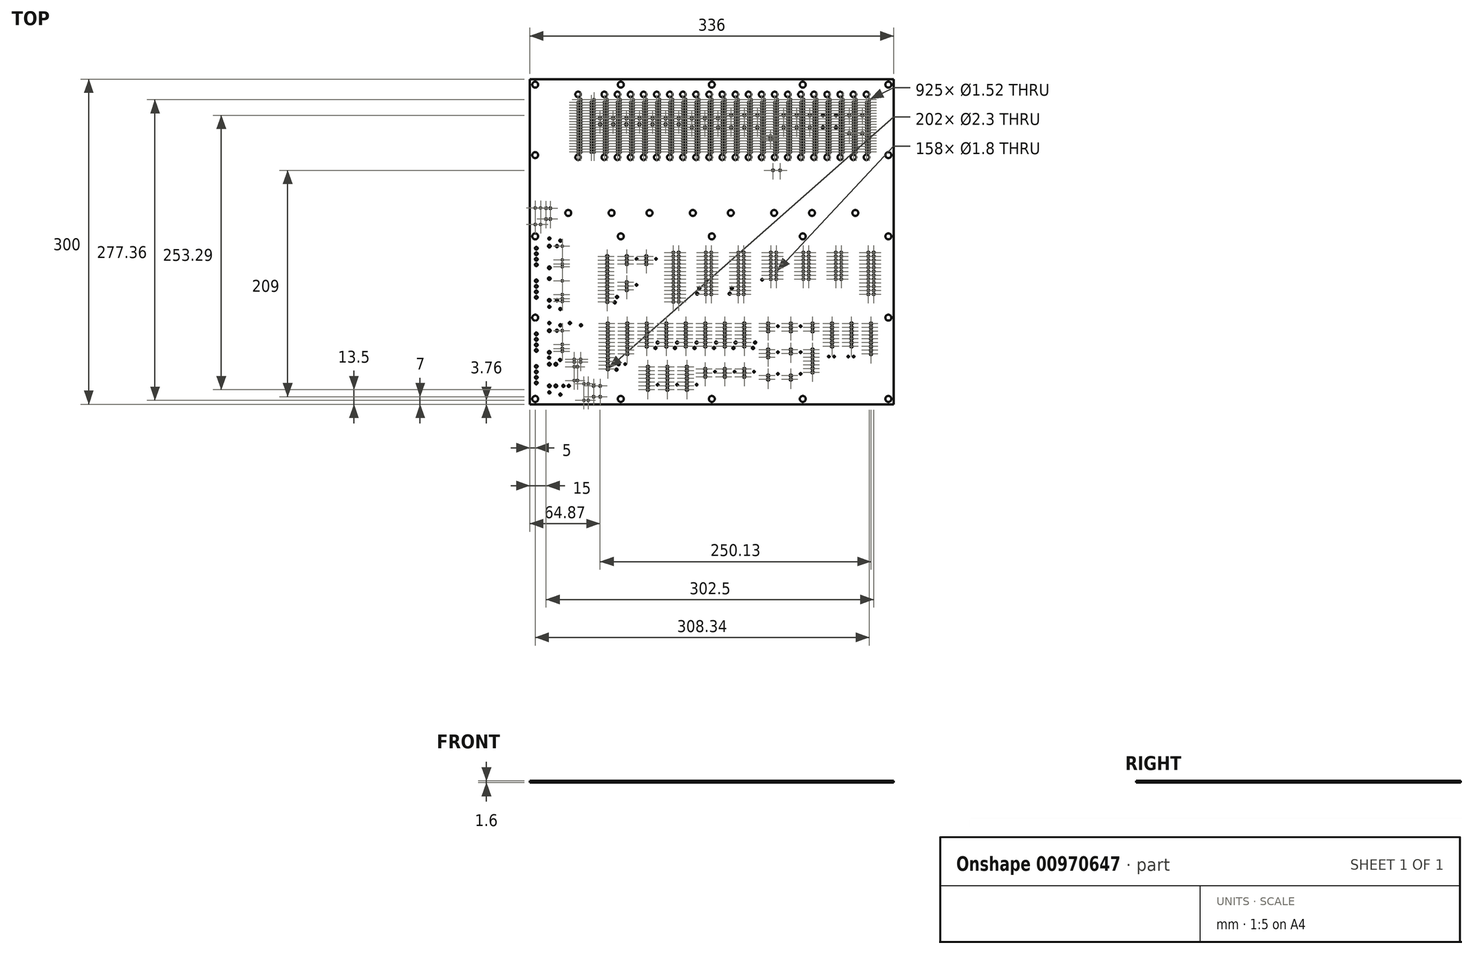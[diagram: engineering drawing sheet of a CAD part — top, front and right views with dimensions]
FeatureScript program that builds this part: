
annotation { "Feature Type Name" : "Feature", "Feature Type Description" : "" }
export const myFeature = defineFeature(function(context is Context, id is Id, definition is map)
    precondition{}
    {
        {
            var Q0;
            Q0=qCreatedBy(makeId("Top.planeOp"),FACE);
            var sketch = newSketch(context, id + "F0", { "sketchPlane" : qUnion([Q0])});
            skCircle(sketch, "E0", {"center": v(-149, 21) * mm, "radius": 0.9 * mm});
            skCircle(sketch, "E1", {"center": v(-149, 31) * mm, "radius": 0.9 * mm});
            skCircle(sketch, "E2", {"center": v(-153, 21) * mm, "radius": 0.9 * mm});
            skCircle(sketch, "E3", {"center": v(-153, 31) * mm, "radius": 0.9 * mm});
            skCircle(sketch, "E4", {"center": v(-103, -133) * mm, "radius": 0.9 * mm});
            skCircle(sketch, "E5", {"center": v(-103, -143) * mm, "radius": 0.9 * mm});
            skCircle(sketch, "E6", {"center": v(-109, -133) * mm, "radius": 0.9 * mm});
            skCircle(sketch, "E7", {"center": v(-109, -143) * mm, "radius": 0.9 * mm});
            skCircle(sketch, "E8", {"center": v(63, 66) * mm, "radius": 0.9 * mm});
            skCircle(sketch, "E9", {"center": v(56.5, 66) * mm, "radius": 0.9 * mm});
            skCircle(sketch, "E10", {"center": v(-162, -6) * mm, "radius": 1.27 * mm});
            skCircle(sketch, "E11", {"center": v(-162, -11.08) * mm, "radius": 1.27 * mm});
            skCircle(sketch, "E12", {"center": v(-162, -16.16) * mm, "radius": 1.27 * mm});
            skCircle(sketch, "E13", {"center": v(-162, -21.24) * mm, "radius": 1.27 * mm});
            skCircle(sketch, "E14", {"center": v(-162, -85) * mm, "radius": 1.27 * mm});
            skCircle(sketch, "E15", {"center": v(-162, -90.08) * mm, "radius": 1.27 * mm});
            skCircle(sketch, "E16", {"center": v(-162, -95.16) * mm, "radius": 1.27 * mm});
            skCircle(sketch, "E17", {"center": v(-162, -100.24) * mm, "radius": 1.27 * mm});
            skCircle(sketch, "E18", {"center": v(-162, -115) * mm, "radius": 1.27 * mm});
            skCircle(sketch, "E19", {"center": v(-162, -120.08) * mm, "radius": 1.27 * mm});
            skCircle(sketch, "E20", {"center": v(-162, -125.16) * mm, "radius": 1.27 * mm});
            skCircle(sketch, "E21", {"center": v(-162, -130.24) * mm, "radius": 1.27 * mm});
            skCircle(sketch, "E22", {"center": v(-162, -36) * mm, "radius": 1.27 * mm});
            skCircle(sketch, "E23", {"center": v(-162, -41.08) * mm, "radius": 1.27 * mm});
            skCircle(sketch, "E24", {"center": v(-162, -46.16) * mm, "radius": 1.27 * mm});
            skCircle(sketch, "E25", {"center": v(-162, -51.24) * mm, "radius": 1.27 * mm});
            skCircle(sketch, "E26", {"center": v(-78.5, -13.4) * mm, "radius": 1.15 * mm});
            skCircle(sketch, "E27", {"center": v(-78.5, -16.9) * mm, "radius": 1.15 * mm});
            skCircle(sketch, "E28", {"center": v(-78.5, -20.4) * mm, "radius": 1.15 * mm});
            skCircle(sketch, "E29", {"center": v(-60.5, -13.4) * mm, "radius": 1.15 * mm});
            skCircle(sketch, "E30", {"center": v(-60.5, -16.9) * mm, "radius": 1.15 * mm});
            skCircle(sketch, "E31", {"center": v(-60.5, -20.4) * mm, "radius": 1.15 * mm});
            skCircle(sketch, "E32", {"center": v(-78.5, -37.4) * mm, "radius": 1.15 * mm});
            skCircle(sketch, "E33", {"center": v(-78.5, -40.9) * mm, "radius": 1.15 * mm});
            skCircle(sketch, "E34", {"center": v(-78.5, -44.4) * mm, "radius": 1.15 * mm});
            skCircle(sketch, "E35", {"center": v(-96.5, -13.4) * mm, "radius": 1.15 * mm});
            skCircle(sketch, "E36", {"center": v(-96.5, -16.9) * mm, "radius": 1.15 * mm});
            skCircle(sketch, "E37", {"center": v(-96.5, -20.4) * mm, "radius": 1.15 * mm});
            skCircle(sketch, "E38", {"center": v(-96.5, -23.9) * mm, "radius": 1.15 * mm});
            skCircle(sketch, "E39", {"center": v(-96.5, -27.4) * mm, "radius": 1.15 * mm});
            skCircle(sketch, "E40", {"center": v(-96.5, -30.9) * mm, "radius": 1.15 * mm});
            skCircle(sketch, "E41", {"center": v(-96.5, -34.4) * mm, "radius": 1.15 * mm});
            skCircle(sketch, "E42", {"center": v(-96.5, -37.9) * mm, "radius": 1.15 * mm});
            skCircle(sketch, "E43", {"center": v(-96.5, -41.4) * mm, "radius": 1.15 * mm});
            skCircle(sketch, "E44", {"center": v(-96.5, -44.9) * mm, "radius": 1.15 * mm});
            skCircle(sketch, "E45", {"center": v(-96.5, -48.4) * mm, "radius": 1.15 * mm});
            skCircle(sketch, "E46", {"center": v(-96.5, -51.9) * mm, "radius": 1.15 * mm});
            skCircle(sketch, "E47", {"center": v(-96.5, -55.4) * mm, "radius": 1.15 * mm});
            skCircle(sketch, "E48", {"center": v(-78, -75.5) * mm, "radius": 1.15 * mm});
            skCircle(sketch, "E49", {"center": v(-78, -79) * mm, "radius": 1.15 * mm});
            skCircle(sketch, "E50", {"center": v(-78, -82.5) * mm, "radius": 1.15 * mm});
            skCircle(sketch, "E51", {"center": v(-78, -86) * mm, "radius": 1.15 * mm});
            skCircle(sketch, "E52", {"center": v(-78, -89.5) * mm, "radius": 1.15 * mm});
            skCircle(sketch, "E53", {"center": v(-78, -93) * mm, "radius": 1.15 * mm});
            skCircle(sketch, "E54", {"center": v(-78, -96.5) * mm, "radius": 1.15 * mm});
            skCircle(sketch, "E55", {"center": v(-78, -100) * mm, "radius": 1.15 * mm});
            skCircle(sketch, "E56", {"center": v(-78, -103.5) * mm, "radius": 1.15 * mm});
            skCircle(sketch, "E57", {"center": v(-60, -75.5) * mm, "radius": 1.15 * mm});
            skCircle(sketch, "E58", {"center": v(-60, -79) * mm, "radius": 1.15 * mm});
            skCircle(sketch, "E59", {"center": v(-60, -82.5) * mm, "radius": 1.15 * mm});
            skCircle(sketch, "E60", {"center": v(-60, -86) * mm, "radius": 1.15 * mm});
            skCircle(sketch, "E61", {"center": v(-60, -89.5) * mm, "radius": 1.15 * mm});
            skCircle(sketch, "E62", {"center": v(-60, -93) * mm, "radius": 1.15 * mm});
            skCircle(sketch, "E63", {"center": v(-60, -96.5) * mm, "radius": 1.15 * mm});
            skCircle(sketch, "E64", {"center": v(-42, -75.5) * mm, "radius": 1.15 * mm});
            skCircle(sketch, "E65", {"center": v(-42, -79) * mm, "radius": 1.15 * mm});
            skCircle(sketch, "E66", {"center": v(-42, -82.5) * mm, "radius": 1.15 * mm});
            skCircle(sketch, "E67", {"center": v(-42, -86) * mm, "radius": 1.15 * mm});
            skCircle(sketch, "E68", {"center": v(-42, -89.5) * mm, "radius": 1.15 * mm});
            skCircle(sketch, "E69", {"center": v(-42, -93) * mm, "radius": 1.15 * mm});
            skCircle(sketch, "E70", {"center": v(-42, -96.5) * mm, "radius": 1.15 * mm});
            skCircle(sketch, "E71", {"center": v(-24, -75.5) * mm, "radius": 1.15 * mm});
            skCircle(sketch, "E72", {"center": v(-24, -79) * mm, "radius": 1.15 * mm});
            skCircle(sketch, "E73", {"center": v(-24, -82.5) * mm, "radius": 1.15 * mm});
            skCircle(sketch, "E74", {"center": v(-24, -86) * mm, "radius": 1.15 * mm});
            skCircle(sketch, "E75", {"center": v(-24, -89.5) * mm, "radius": 1.15 * mm});
            skCircle(sketch, "E76", {"center": v(-24, -93) * mm, "radius": 1.15 * mm});
            skCircle(sketch, "E77", {"center": v(-24, -96.5) * mm, "radius": 1.15 * mm});
            skCircle(sketch, "E78", {"center": v(-6, -75.5) * mm, "radius": 1.15 * mm});
            skCircle(sketch, "E79", {"center": v(-6, -79) * mm, "radius": 1.15 * mm});
            skCircle(sketch, "E80", {"center": v(-6, -82.5) * mm, "radius": 1.15 * mm});
            skCircle(sketch, "E81", {"center": v(-6, -86) * mm, "radius": 1.15 * mm});
            skCircle(sketch, "E82", {"center": v(-6, -89.5) * mm, "radius": 1.15 * mm});
            skCircle(sketch, "E83", {"center": v(-6, -93) * mm, "radius": 1.15 * mm});
            skCircle(sketch, "E84", {"center": v(-6, -96.5) * mm, "radius": 1.15 * mm});
            skCircle(sketch, "E85", {"center": v(12, -75.5) * mm, "radius": 1.15 * mm});
            skCircle(sketch, "E86", {"center": v(12, -79) * mm, "radius": 1.15 * mm});
            skCircle(sketch, "E87", {"center": v(12, -82.5) * mm, "radius": 1.15 * mm});
            skCircle(sketch, "E88", {"center": v(12, -86) * mm, "radius": 1.15 * mm});
            skCircle(sketch, "E89", {"center": v(12, -89.5) * mm, "radius": 1.15 * mm});
            skCircle(sketch, "E90", {"center": v(12, -93) * mm, "radius": 1.15 * mm});
            skCircle(sketch, "E91", {"center": v(12, -96.5) * mm, "radius": 1.15 * mm});
            skCircle(sketch, "E92", {"center": v(30, -75.5) * mm, "radius": 1.15 * mm});
            skCircle(sketch, "E93", {"center": v(30, -79) * mm, "radius": 1.15 * mm});
            skCircle(sketch, "E94", {"center": v(30, -82.5) * mm, "radius": 1.15 * mm});
            skCircle(sketch, "E95", {"center": v(30, -86) * mm, "radius": 1.15 * mm});
            skCircle(sketch, "E96", {"center": v(30, -89.5) * mm, "radius": 1.15 * mm});
            skCircle(sketch, "E97", {"center": v(30, -93) * mm, "radius": 1.15 * mm});
            skCircle(sketch, "E98", {"center": v(30, -96.5) * mm, "radius": 1.15 * mm});
            skCircle(sketch, "E99", {"center": v(-96, -75.5) * mm, "radius": 1.15 * mm});
            skCircle(sketch, "E100", {"center": v(-96, -79) * mm, "radius": 1.15 * mm});
            skCircle(sketch, "E101", {"center": v(-96, -82.5) * mm, "radius": 1.15 * mm});
            skCircle(sketch, "E102", {"center": v(-96, -86) * mm, "radius": 1.15 * mm});
            skCircle(sketch, "E103", {"center": v(-96, -89.5) * mm, "radius": 1.15 * mm});
            skCircle(sketch, "E104", {"center": v(-96, -93) * mm, "radius": 1.15 * mm});
            skCircle(sketch, "E105", {"center": v(-96, -96.5) * mm, "radius": 1.15 * mm});
            skCircle(sketch, "E106", {"center": v(-96, -100) * mm, "radius": 1.15 * mm});
            skCircle(sketch, "E107", {"center": v(-96, -103.5) * mm, "radius": 1.15 * mm});
            skCircle(sketch, "E108", {"center": v(-96, -107) * mm, "radius": 1.15 * mm});
            skCircle(sketch, "E109", {"center": v(-96, -110.5) * mm, "radius": 1.15 * mm});
            skCircle(sketch, "E110", {"center": v(-96, -114) * mm, "radius": 1.15 * mm});
            skCircle(sketch, "E111", {"center": v(-96, -117.5) * mm, "radius": 1.15 * mm});
            skCircle(sketch, "E112", {"center": v(-6, -117.5) * mm, "radius": 1.15 * mm});
            skCircle(sketch, "E113", {"center": v(-6, -121) * mm, "radius": 1.15 * mm});
            skCircle(sketch, "E114", {"center": v(-6, -124.5) * mm, "radius": 1.15 * mm});
            skCircle(sketch, "E115", {"center": v(12, -117.5) * mm, "radius": 1.15 * mm});
            skCircle(sketch, "E116", {"center": v(12, -121) * mm, "radius": 1.15 * mm});
            skCircle(sketch, "E117", {"center": v(12, -124.5) * mm, "radius": 1.15 * mm});
            skCircle(sketch, "E118", {"center": v(30, -117.5) * mm, "radius": 1.15 * mm});
            skCircle(sketch, "E119", {"center": v(30, -121) * mm, "radius": 1.15 * mm});
            skCircle(sketch, "E120", {"center": v(30, -124.5) * mm, "radius": 1.15 * mm});
            skCircle(sketch, "E121", {"center": v(52, -75.5) * mm, "radius": 1.15 * mm});
            skCircle(sketch, "E122", {"center": v(52, -79) * mm, "radius": 1.15 * mm});
            skCircle(sketch, "E123", {"center": v(52, -82.5) * mm, "radius": 1.15 * mm});
            skCircle(sketch, "E124", {"center": v(73, -75.5) * mm, "radius": 1.15 * mm});
            skCircle(sketch, "E125", {"center": v(73, -79) * mm, "radius": 1.15 * mm});
            skCircle(sketch, "E126", {"center": v(73, -82.5) * mm, "radius": 1.15 * mm});
            skCircle(sketch, "E127", {"center": v(52, -99.5) * mm, "radius": 1.15 * mm});
            skCircle(sketch, "E128", {"center": v(52, -103) * mm, "radius": 1.15 * mm});
            skCircle(sketch, "E129", {"center": v(52, -106.5) * mm, "radius": 1.15 * mm});
            skCircle(sketch, "E130", {"center": v(73, -99.5) * mm, "radius": 1.15 * mm});
            skCircle(sketch, "E131", {"center": v(73, -103) * mm, "radius": 1.15 * mm});
            skCircle(sketch, "E132", {"center": v(52, -123.5) * mm, "radius": 1.15 * mm});
            skCircle(sketch, "E133", {"center": v(52, -127) * mm, "radius": 1.15 * mm});
            skCircle(sketch, "E134", {"center": v(73, -123.5) * mm, "radius": 1.15 * mm});
            skCircle(sketch, "E135", {"center": v(73, -127) * mm, "radius": 1.15 * mm});
            skCircle(sketch, "E136", {"center": v(-59, -115.5) * mm, "radius": 1.15 * mm});
            skCircle(sketch, "E137", {"center": v(-59, -119) * mm, "radius": 1.15 * mm});
            skCircle(sketch, "E138", {"center": v(-59, -122.5) * mm, "radius": 1.15 * mm});
            skCircle(sketch, "E139", {"center": v(-59, -126) * mm, "radius": 1.15 * mm});
            skCircle(sketch, "E140", {"center": v(-59, -129.5) * mm, "radius": 1.15 * mm});
            skCircle(sketch, "E141", {"center": v(-59, -133) * mm, "radius": 1.15 * mm});
            skCircle(sketch, "E142", {"center": v(-59, -136.5) * mm, "radius": 1.15 * mm});
            skCircle(sketch, "E143", {"center": v(-23, -115.5) * mm, "radius": 1.15 * mm});
            skCircle(sketch, "E144", {"center": v(-23, -119) * mm, "radius": 1.15 * mm});
            skCircle(sketch, "E145", {"center": v(-23, -122.5) * mm, "radius": 1.15 * mm});
            skCircle(sketch, "E146", {"center": v(-23, -126) * mm, "radius": 1.15 * mm});
            skCircle(sketch, "E147", {"center": v(-23, -129.5) * mm, "radius": 1.15 * mm});
            skCircle(sketch, "E148", {"center": v(-23, -133) * mm, "radius": 1.15 * mm});
            skCircle(sketch, "E149", {"center": v(-23, -136.5) * mm, "radius": 1.15 * mm});
            skCircle(sketch, "E150", {"center": v(-41, -115.5) * mm, "radius": 1.15 * mm});
            skCircle(sketch, "E151", {"center": v(-41, -119) * mm, "radius": 1.15 * mm});
            skCircle(sketch, "E152", {"center": v(-41, -122.5) * mm, "radius": 1.15 * mm});
            skCircle(sketch, "E153", {"center": v(-41, -126) * mm, "radius": 1.15 * mm});
            skCircle(sketch, "E154", {"center": v(-41, -129.5) * mm, "radius": 1.15 * mm});
            skCircle(sketch, "E155", {"center": v(-41, -133) * mm, "radius": 1.15 * mm});
            skCircle(sketch, "E156", {"center": v(-41, -136.5) * mm, "radius": 1.15 * mm});
            skCircle(sketch, "E157", {"center": v(93, -75.5) * mm, "radius": 1.15 * mm});
            skCircle(sketch, "E158", {"center": v(93, -79) * mm, "radius": 1.15 * mm});
            skCircle(sketch, "E159", {"center": v(93, -82.5) * mm, "radius": 1.15 * mm});
            skCircle(sketch, "E160", {"center": v(111, -75.5) * mm, "radius": 1.15 * mm});
            skCircle(sketch, "E161", {"center": v(111, -79) * mm, "radius": 1.15 * mm});
            skCircle(sketch, "E162", {"center": v(111, -82.5) * mm, "radius": 1.15 * mm});
            skCircle(sketch, "E163", {"center": v(111, -86) * mm, "radius": 1.15 * mm});
            skCircle(sketch, "E164", {"center": v(111, -89.5) * mm, "radius": 1.15 * mm});
            skCircle(sketch, "E165", {"center": v(111, -93) * mm, "radius": 1.15 * mm});
            skCircle(sketch, "E166", {"center": v(111, -96.5) * mm, "radius": 1.15 * mm});
            skCircle(sketch, "E167", {"center": v(129, -75.5) * mm, "radius": 1.15 * mm});
            skCircle(sketch, "E168", {"center": v(129, -79) * mm, "radius": 1.15 * mm});
            skCircle(sketch, "E169", {"center": v(129, -82.5) * mm, "radius": 1.15 * mm});
            skCircle(sketch, "E170", {"center": v(129, -86) * mm, "radius": 1.15 * mm});
            skCircle(sketch, "E171", {"center": v(129, -89.5) * mm, "radius": 1.15 * mm});
            skCircle(sketch, "E172", {"center": v(129, -93) * mm, "radius": 1.15 * mm});
            skCircle(sketch, "E173", {"center": v(129, -96.5) * mm, "radius": 1.15 * mm});
            skCircle(sketch, "E174", {"center": v(147, -75.5) * mm, "radius": 1.15 * mm});
            skCircle(sketch, "E175", {"center": v(147, -79) * mm, "radius": 1.15 * mm});
            skCircle(sketch, "E176", {"center": v(147, -82.5) * mm, "radius": 1.15 * mm});
            skCircle(sketch, "E177", {"center": v(147, -86) * mm, "radius": 1.15 * mm});
            skCircle(sketch, "E178", {"center": v(147, -89.5) * mm, "radius": 1.15 * mm});
            skCircle(sketch, "E179", {"center": v(147, -93) * mm, "radius": 1.15 * mm});
            skCircle(sketch, "E180", {"center": v(147, -96.5) * mm, "radius": 1.15 * mm});
            skCircle(sketch, "E181", {"center": v(147, -100) * mm, "radius": 1.15 * mm});
            skCircle(sketch, "E182", {"center": v(147, -103.5) * mm, "radius": 1.15 * mm});
            skCircle(sketch, "E183", {"center": v(93, -99.5) * mm, "radius": 1.15 * mm});
            skCircle(sketch, "E184", {"center": v(93, -103) * mm, "radius": 1.15 * mm});
            skCircle(sketch, "E185", {"center": v(93, -106.5) * mm, "radius": 1.15 * mm});
            skCircle(sketch, "E186", {"center": v(93, -110) * mm, "radius": 1.15 * mm});
            skCircle(sketch, "E187", {"center": v(93, -113.5) * mm, "radius": 1.15 * mm});
            skCircle(sketch, "E188", {"center": v(93, -117) * mm, "radius": 1.15 * mm});
            skCircle(sketch, "E189", {"center": v(93, -120.5) * mm, "radius": 1.15 * mm});
            skCircle(sketch, "E190", {"center": v(-18.43, 114) * mm, "radius": 1.15 * mm});
            skCircle(sketch, "E191", {"center": v(-18.43, 105.6) * mm, "radius": 1.15 * mm});
            skCircle(sketch, "E192", {"center": v(5.77, 114) * mm, "radius": 1.15 * mm});
            skCircle(sketch, "E193", {"center": v(5.77, 105.6) * mm, "radius": 1.15 * mm});
            skCircle(sketch, "E194", {"center": v(17.87, 116.79) * mm, "radius": 1.15 * mm});
            skCircle(sketch, "E195", {"center": v(17.87, 105.6) * mm, "radius": 1.15 * mm});
            skCircle(sketch, "E196", {"center": v(29.97, 116.79) * mm, "radius": 1.15 * mm});
            skCircle(sketch, "E197", {"center": v(29.97, 105.6) * mm, "radius": 1.15 * mm});
            skCircle(sketch, "E198", {"center": v(42.07, 116.79) * mm, "radius": 1.15 * mm});
            skCircle(sketch, "E199", {"center": v(42.07, 105.6) * mm, "radius": 1.15 * mm});
            skCircle(sketch, "E200", {"center": v(54.17, 97.2) * mm, "radius": 1.15 * mm});
            skCircle(sketch, "E201", {"center": v(54.17, 94.39) * mm, "radius": 1.15 * mm});
            skCircle(sketch, "E202", {"center": v(66.27, 116.79) * mm, "radius": 1.15 * mm});
            skCircle(sketch, "E203", {"center": v(66.27, 105.6) * mm, "radius": 1.15 * mm});
            skCircle(sketch, "E204", {"center": v(-6.33, 114) * mm, "radius": 1.15 * mm});
            skCircle(sketch, "E205", {"center": v(-6.33, 105.6) * mm, "radius": 1.15 * mm});
            skCircle(sketch, "E206", {"center": v(78.37, 116.79) * mm, "radius": 1.15 * mm});
            skCircle(sketch, "E207", {"center": v(78.37, 105.6) * mm, "radius": 1.15 * mm});
            skCircle(sketch, "E208", {"center": v(90.47, 116.79) * mm, "radius": 1.15 * mm});
            skCircle(sketch, "E209", {"center": v(90.47, 105.6) * mm, "radius": 1.15 * mm});
            skCircle(sketch, "E210", {"center": v(-103.13, 114) * mm, "radius": 1.15 * mm});
            skCircle(sketch, "E211", {"center": v(-103.13, 108.39) * mm, "radius": 1.15 * mm});
            skCircle(sketch, "E212", {"center": v(126.8, 116.79) * mm, "radius": 1.15 * mm});
            skCircle(sketch, "E213", {"center": v(126.8, 99.99) * mm, "radius": 1.15 * mm});
            skCircle(sketch, "E214", {"center": v(138.9, 116.79) * mm, "radius": 1.15 * mm});
            skCircle(sketch, "E215", {"center": v(138.9, 99.99) * mm, "radius": 1.15 * mm});
            skCircle(sketch, "E216", {"center": v(-91.03, 114) * mm, "radius": 1.15 * mm});
            skCircle(sketch, "E217", {"center": v(-91.03, 108.39) * mm, "radius": 1.15 * mm});
            skCircle(sketch, "E218", {"center": v(-78.93, 114) * mm, "radius": 1.15 * mm});
            skCircle(sketch, "E219", {"center": v(-78.93, 108.39) * mm, "radius": 1.15 * mm});
            skCircle(sketch, "E220", {"center": v(-66.83, 114) * mm, "radius": 1.15 * mm});
            skCircle(sketch, "E221", {"center": v(-66.83, 108.39) * mm, "radius": 1.15 * mm});
            skCircle(sketch, "E222", {"center": v(-54.73, 114) * mm, "radius": 1.15 * mm});
            skCircle(sketch, "E223", {"center": v(-54.73, 108.39) * mm, "radius": 1.15 * mm});
            skCircle(sketch, "E224", {"center": v(-42.63, 114) * mm, "radius": 1.15 * mm});
            skCircle(sketch, "E225", {"center": v(-42.63, 108.39) * mm, "radius": 1.15 * mm});
            skCircle(sketch, "E226", {"center": v(-30.53, 114) * mm, "radius": 1.15 * mm});
            skCircle(sketch, "E227", {"center": v(-30.53, 108.39) * mm, "radius": 1.15 * mm});
            skCircle(sketch, "E228", {"center": v(-30.5, -9.9) * mm, "radius": 0.9 * mm});
            skCircle(sketch, "E229", {"center": v(-30.5, -13.4) * mm, "radius": 0.9 * mm});
            skCircle(sketch, "E230", {"center": v(-30.5, -16.9) * mm, "radius": 0.9 * mm});
            skCircle(sketch, "E231", {"center": v(-30.5, -20.4) * mm, "radius": 0.9 * mm});
            skCircle(sketch, "E232", {"center": v(-30.5, -23.9) * mm, "radius": 0.9 * mm});
            skCircle(sketch, "E233", {"center": v(-30.5, -27.4) * mm, "radius": 0.9 * mm});
            skCircle(sketch, "E234", {"center": v(-30.5, -30.9) * mm, "radius": 0.9 * mm});
            skCircle(sketch, "E235", {"center": v(-30.5, -34.4) * mm, "radius": 0.9 * mm});
            skCircle(sketch, "E236", {"center": v(-30.5, -37.9) * mm, "radius": 0.9 * mm});
            skCircle(sketch, "E237", {"center": v(-30.5, -41.4) * mm, "radius": 0.9 * mm});
            skCircle(sketch, "E238", {"center": v(-30.5, -44.9) * mm, "radius": 0.9 * mm});
            skCircle(sketch, "E239", {"center": v(-30.5, -48.4) * mm, "radius": 0.9 * mm});
            skCircle(sketch, "E240", {"center": v(-30.5, -51.9) * mm, "radius": 0.9 * mm});
            skCircle(sketch, "E241", {"center": v(-30.5, -55.4) * mm, "radius": 0.9 * mm});
            skCircle(sketch, "E242", {"center": v(-35.5, -9.9) * mm, "radius": 0.9 * mm});
            skCircle(sketch, "E243", {"center": v(-35.5, -13.4) * mm, "radius": 0.9 * mm});
            skCircle(sketch, "E244", {"center": v(-35.5, -16.9) * mm, "radius": 0.9 * mm});
            skCircle(sketch, "E245", {"center": v(-35.5, -20.4) * mm, "radius": 0.9 * mm});
            skCircle(sketch, "E246", {"center": v(-35.5, -23.9) * mm, "radius": 0.9 * mm});
            skCircle(sketch, "E247", {"center": v(-35.5, -27.4) * mm, "radius": 0.9 * mm});
            skCircle(sketch, "E248", {"center": v(-35.5, -30.9) * mm, "radius": 0.9 * mm});
            skCircle(sketch, "E249", {"center": v(-35.5, -34.4) * mm, "radius": 0.9 * mm});
            skCircle(sketch, "E250", {"center": v(-35.5, -37.9) * mm, "radius": 0.9 * mm});
            skCircle(sketch, "E251", {"center": v(-35.5, -41.4) * mm, "radius": 0.9 * mm});
            skCircle(sketch, "E252", {"center": v(-35.5, -44.9) * mm, "radius": 0.9 * mm});
            skCircle(sketch, "E253", {"center": v(-35.5, -48.4) * mm, "radius": 0.9 * mm});
            skCircle(sketch, "E254", {"center": v(-35.5, -51.9) * mm, "radius": 0.9 * mm});
            skCircle(sketch, "E255", {"center": v(-35.5, -55.4) * mm, "radius": 0.9 * mm});
            skCircle(sketch, "E256", {"center": v(89.5, -9.9) * mm, "radius": 0.9 * mm});
            skCircle(sketch, "E257", {"center": v(89.5, -13.4) * mm, "radius": 0.9 * mm});
            skCircle(sketch, "E258", {"center": v(89.5, -16.9) * mm, "radius": 0.9 * mm});
            skCircle(sketch, "E259", {"center": v(89.5, -20.4) * mm, "radius": 0.9 * mm});
            skCircle(sketch, "E260", {"center": v(89.5, -23.9) * mm, "radius": 0.9 * mm});
            skCircle(sketch, "E261", {"center": v(89.5, -27.4) * mm, "radius": 0.9 * mm});
            skCircle(sketch, "E262", {"center": v(89.5, -30.9) * mm, "radius": 0.9 * mm});
            skCircle(sketch, "E263", {"center": v(89.5, -34.4) * mm, "radius": 0.9 * mm});
            skCircle(sketch, "E264", {"center": v(84.5, -9.9) * mm, "radius": 0.9 * mm});
            skCircle(sketch, "E265", {"center": v(84.5, -13.4) * mm, "radius": 0.9 * mm});
            skCircle(sketch, "E266", {"center": v(84.5, -16.9) * mm, "radius": 0.9 * mm});
            skCircle(sketch, "E267", {"center": v(84.5, -20.4) * mm, "radius": 0.9 * mm});
            skCircle(sketch, "E268", {"center": v(84.5, -23.9) * mm, "radius": 0.9 * mm});
            skCircle(sketch, "E269", {"center": v(84.5, -27.4) * mm, "radius": 0.9 * mm});
            skCircle(sketch, "E270", {"center": v(84.5, -30.9) * mm, "radius": 0.9 * mm});
            skCircle(sketch, "E271", {"center": v(84.5, -34.4) * mm, "radius": 0.9 * mm});
            skCircle(sketch, "E272", {"center": v(-0.5, -9.9) * mm, "radius": 0.9 * mm});
            skCircle(sketch, "E273", {"center": v(-0.5, -13.4) * mm, "radius": 0.9 * mm});
            skCircle(sketch, "E274", {"center": v(-0.5, -16.9) * mm, "radius": 0.9 * mm});
            skCircle(sketch, "E275", {"center": v(-0.5, -20.4) * mm, "radius": 0.9 * mm});
            skCircle(sketch, "E276", {"center": v(-0.5, -23.9) * mm, "radius": 0.9 * mm});
            skCircle(sketch, "E277", {"center": v(-0.5, -27.4) * mm, "radius": 0.9 * mm});
            skCircle(sketch, "E278", {"center": v(-0.5, -30.9) * mm, "radius": 0.9 * mm});
            skCircle(sketch, "E279", {"center": v(-0.5, -34.4) * mm, "radius": 0.9 * mm});
            skCircle(sketch, "E280", {"center": v(-0.5, -37.9) * mm, "radius": 0.9 * mm});
            skCircle(sketch, "E281", {"center": v(-0.5, -41.4) * mm, "radius": 0.9 * mm});
            skCircle(sketch, "E282", {"center": v(-0.5, -44.9) * mm, "radius": 0.9 * mm});
            skCircle(sketch, "E283", {"center": v(-0.5, -48.4) * mm, "radius": 0.9 * mm});
            skCircle(sketch, "E284", {"center": v(-5.5, -9.9) * mm, "radius": 0.9 * mm});
            skCircle(sketch, "E285", {"center": v(-5.5, -13.4) * mm, "radius": 0.9 * mm});
            skCircle(sketch, "E286", {"center": v(-5.5, -16.9) * mm, "radius": 0.9 * mm});
            skCircle(sketch, "E287", {"center": v(-5.5, -20.4) * mm, "radius": 0.9 * mm});
            skCircle(sketch, "E288", {"center": v(-5.5, -23.9) * mm, "radius": 0.9 * mm});
            skCircle(sketch, "E289", {"center": v(-5.5, -27.4) * mm, "radius": 0.9 * mm});
            skCircle(sketch, "E290", {"center": v(-5.5, -30.9) * mm, "radius": 0.9 * mm});
            skCircle(sketch, "E291", {"center": v(-5.5, -34.4) * mm, "radius": 0.9 * mm});
            skCircle(sketch, "E292", {"center": v(-5.5, -37.9) * mm, "radius": 0.9 * mm});
            skCircle(sketch, "E293", {"center": v(-5.5, -41.4) * mm, "radius": 0.9 * mm});
            skCircle(sketch, "E294", {"center": v(-5.5, -44.9) * mm, "radius": 0.9 * mm});
            skCircle(sketch, "E295", {"center": v(-5.5, -48.4) * mm, "radius": 0.9 * mm});
            skCircle(sketch, "E296", {"center": v(29.5, -9.9) * mm, "radius": 0.9 * mm});
            skCircle(sketch, "E297", {"center": v(29.5, -13.4) * mm, "radius": 0.9 * mm});
            skCircle(sketch, "E298", {"center": v(29.5, -16.9) * mm, "radius": 0.9 * mm});
            skCircle(sketch, "E299", {"center": v(29.5, -20.4) * mm, "radius": 0.9 * mm});
            skCircle(sketch, "E300", {"center": v(29.5, -23.9) * mm, "radius": 0.9 * mm});
            skCircle(sketch, "E301", {"center": v(29.5, -27.4) * mm, "radius": 0.9 * mm});
            skCircle(sketch, "E302", {"center": v(29.5, -30.9) * mm, "radius": 0.9 * mm});
            skCircle(sketch, "E303", {"center": v(29.5, -34.4) * mm, "radius": 0.9 * mm});
            skCircle(sketch, "E304", {"center": v(29.5, -37.9) * mm, "radius": 0.9 * mm});
            skCircle(sketch, "E305", {"center": v(29.5, -41.4) * mm, "radius": 0.9 * mm});
            skCircle(sketch, "E306", {"center": v(29.5, -44.9) * mm, "radius": 0.9 * mm});
            skCircle(sketch, "E307", {"center": v(29.5, -48.4) * mm, "radius": 0.9 * mm});
            skCircle(sketch, "E308", {"center": v(24.5, -9.9) * mm, "radius": 0.9 * mm});
            skCircle(sketch, "E309", {"center": v(24.5, -13.4) * mm, "radius": 0.9 * mm});
            skCircle(sketch, "E310", {"center": v(24.5, -16.9) * mm, "radius": 0.9 * mm});
            skCircle(sketch, "E311", {"center": v(24.5, -20.4) * mm, "radius": 0.9 * mm});
            skCircle(sketch, "E312", {"center": v(24.5, -23.9) * mm, "radius": 0.9 * mm});
            skCircle(sketch, "E313", {"center": v(24.5, -27.4) * mm, "radius": 0.9 * mm});
            skCircle(sketch, "E314", {"center": v(24.5, -30.9) * mm, "radius": 0.9 * mm});
            skCircle(sketch, "E315", {"center": v(24.5, -34.4) * mm, "radius": 0.9 * mm});
            skCircle(sketch, "E316", {"center": v(24.5, -37.9) * mm, "radius": 0.9 * mm});
            skCircle(sketch, "E317", {"center": v(24.5, -41.4) * mm, "radius": 0.9 * mm});
            skCircle(sketch, "E318", {"center": v(24.5, -44.9) * mm, "radius": 0.9 * mm});
            skCircle(sketch, "E319", {"center": v(24.5, -48.4) * mm, "radius": 0.9 * mm});
            skCircle(sketch, "E320", {"center": v(59.5, -9.9) * mm, "radius": 0.9 * mm});
            skCircle(sketch, "E321", {"center": v(59.5, -13.4) * mm, "radius": 0.9 * mm});
            skCircle(sketch, "E322", {"center": v(59.5, -16.9) * mm, "radius": 0.9 * mm});
            skCircle(sketch, "E323", {"center": v(59.5, -20.4) * mm, "radius": 0.9 * mm});
            skCircle(sketch, "E324", {"center": v(59.5, -23.9) * mm, "radius": 0.9 * mm});
            skCircle(sketch, "E325", {"center": v(59.5, -27.4) * mm, "radius": 0.9 * mm});
            skCircle(sketch, "E326", {"center": v(59.5, -30.9) * mm, "radius": 0.9 * mm});
            skCircle(sketch, "E327", {"center": v(59.5, -34.4) * mm, "radius": 0.9 * mm});
            skCircle(sketch, "E328", {"center": v(54.5, -9.9) * mm, "radius": 0.9 * mm});
            skCircle(sketch, "E329", {"center": v(54.5, -13.4) * mm, "radius": 0.9 * mm});
            skCircle(sketch, "E330", {"center": v(54.5, -16.9) * mm, "radius": 0.9 * mm});
            skCircle(sketch, "E331", {"center": v(54.5, -20.4) * mm, "radius": 0.9 * mm});
            skCircle(sketch, "E332", {"center": v(54.5, -23.9) * mm, "radius": 0.9 * mm});
            skCircle(sketch, "E333", {"center": v(54.5, -27.4) * mm, "radius": 0.9 * mm});
            skCircle(sketch, "E334", {"center": v(54.5, -30.9) * mm, "radius": 0.9 * mm});
            skCircle(sketch, "E335", {"center": v(54.5, -34.4) * mm, "radius": 0.9 * mm});
            skCircle(sketch, "E336", {"center": v(119.5, -9.9) * mm, "radius": 0.9 * mm});
            skCircle(sketch, "E337", {"center": v(119.5, -13.4) * mm, "radius": 0.9 * mm});
            skCircle(sketch, "E338", {"center": v(119.5, -16.9) * mm, "radius": 0.9 * mm});
            skCircle(sketch, "E339", {"center": v(119.5, -20.4) * mm, "radius": 0.9 * mm});
            skCircle(sketch, "E340", {"center": v(119.5, -23.9) * mm, "radius": 0.9 * mm});
            skCircle(sketch, "E341", {"center": v(119.5, -27.4) * mm, "radius": 0.9 * mm});
            skCircle(sketch, "E342", {"center": v(119.5, -30.9) * mm, "radius": 0.9 * mm});
            skCircle(sketch, "E343", {"center": v(119.5, -34.4) * mm, "radius": 0.9 * mm});
            skCircle(sketch, "E344", {"center": v(114.5, -9.9) * mm, "radius": 0.9 * mm});
            skCircle(sketch, "E345", {"center": v(114.5, -13.4) * mm, "radius": 0.9 * mm});
            skCircle(sketch, "E346", {"center": v(114.5, -16.9) * mm, "radius": 0.9 * mm});
            skCircle(sketch, "E347", {"center": v(114.5, -20.4) * mm, "radius": 0.9 * mm});
            skCircle(sketch, "E348", {"center": v(114.5, -23.9) * mm, "radius": 0.9 * mm});
            skCircle(sketch, "E349", {"center": v(114.5, -27.4) * mm, "radius": 0.9 * mm});
            skCircle(sketch, "E350", {"center": v(114.5, -30.9) * mm, "radius": 0.9 * mm});
            skCircle(sketch, "E351", {"center": v(114.5, -34.4) * mm, "radius": 0.9 * mm});
            skCircle(sketch, "E352", {"center": v(149.5, -9.9) * mm, "radius": 0.9 * mm});
            skCircle(sketch, "E353", {"center": v(149.5, -13.4) * mm, "radius": 0.9 * mm});
            skCircle(sketch, "E354", {"center": v(149.5, -16.9) * mm, "radius": 0.9 * mm});
            skCircle(sketch, "E355", {"center": v(149.5, -20.4) * mm, "radius": 0.9 * mm});
            skCircle(sketch, "E356", {"center": v(149.5, -23.9) * mm, "radius": 0.9 * mm});
            skCircle(sketch, "E357", {"center": v(149.5, -27.4) * mm, "radius": 0.9 * mm});
            skCircle(sketch, "E358", {"center": v(149.5, -30.9) * mm, "radius": 0.9 * mm});
            skCircle(sketch, "E359", {"center": v(149.5, -34.4) * mm, "radius": 0.9 * mm});
            skCircle(sketch, "E360", {"center": v(149.5, -37.9) * mm, "radius": 0.9 * mm});
            skCircle(sketch, "E361", {"center": v(149.5, -41.4) * mm, "radius": 0.9 * mm});
            skCircle(sketch, "E362", {"center": v(149.5, -44.9) * mm, "radius": 0.9 * mm});
            skCircle(sketch, "E363", {"center": v(149.5, -48.4) * mm, "radius": 0.9 * mm});
            skCircle(sketch, "E364", {"center": v(144.5, -9.9) * mm, "radius": 0.9 * mm});
            skCircle(sketch, "E365", {"center": v(144.5, -13.4) * mm, "radius": 0.9 * mm});
            skCircle(sketch, "E366", {"center": v(144.5, -16.9) * mm, "radius": 0.9 * mm});
            skCircle(sketch, "E367", {"center": v(144.5, -20.4) * mm, "radius": 0.9 * mm});
            skCircle(sketch, "E368", {"center": v(144.5, -23.9) * mm, "radius": 0.9 * mm});
            skCircle(sketch, "E369", {"center": v(144.5, -27.4) * mm, "radius": 0.9 * mm});
            skCircle(sketch, "E370", {"center": v(144.5, -30.9) * mm, "radius": 0.9 * mm});
            skCircle(sketch, "E371", {"center": v(144.5, -34.4) * mm, "radius": 0.9 * mm});
            skCircle(sketch, "E372", {"center": v(144.5, -37.9) * mm, "radius": 0.9 * mm});
            skCircle(sketch, "E373", {"center": v(144.5, -41.4) * mm, "radius": 0.9 * mm});
            skCircle(sketch, "E374", {"center": v(144.5, -44.9) * mm, "radius": 0.9 * mm});
            skCircle(sketch, "E375", {"center": v(144.5, -48.4) * mm, "radius": 0.9 * mm});
            skCircle(sketch, "E376", {"center": v(-150, -24) * mm, "radius": 1.25 * mm});
            skCircle(sketch, "E377", {"center": v(-150, -4) * mm, "radius": 1.25 * mm});
            skCircle(sketch, "E378", {"center": v(-150, -34) * mm, "radius": 1.25 * mm});
            skCircle(sketch, "E379", {"center": v(-150, -54) * mm, "radius": 1.25 * mm});
            skCircle(sketch, "E380", {"center": v(-150, -102) * mm, "radius": 1.25 * mm});
            skCircle(sketch, "E381", {"center": v(-150, -82) * mm, "radius": 1.25 * mm});
            skCircle(sketch, "E382", {"center": v(-150, -113) * mm, "radius": 1.25 * mm});
            skCircle(sketch, "E383", {"center": v(-150, -133) * mm, "radius": 1.25 * mm});
            skCircle(sketch, "E384", {"center": v(-144, -113) * mm, "radius": 1.25 * mm});
            skCircle(sketch, "E385", {"center": v(-144, -133) * mm, "radius": 1.25 * mm});
            skCircle(sketch, "E386", {"center": v(-132, -133) * mm, "radius": 1 * mm});
            skCircle(sketch, "E387", {"center": v(-143, -4) * mm, "radius": 1 * mm});
            skCircle(sketch, "E388", {"center": v(-143, -54) * mm, "radius": 1 * mm});
            skCircle(sketch, "E389", {"center": v(-143, -82) * mm, "radius": 1 * mm});
            skCircle(sketch, "E390", {"center": v(-137, -133) * mm, "radius": 1 * mm});
            skCircle(sketch, "E391", {"center": v(-150, 3) * mm, "radius": 1 * mm});
            skCircle(sketch, "E392", {"center": v(-139.8, 1) * mm, "radius": 1 * mm});
            skCircle(sketch, "E393", {"center": v(-150, -75) * mm, "radius": 1 * mm});
            skCircle(sketch, "E394", {"center": v(-139.8, -77) * mm, "radius": 1 * mm});
            skCircle(sketch, "E395", {"center": v(-150, -139) * mm, "radius": 1 * mm});
            skCircle(sketch, "E396", {"center": v(-139.8, -141) * mm, "radius": 1 * mm});
            skCircle(sketch, "E397", {"center": v(-140, -109) * mm, "radius": 1 * mm});
            skCircle(sketch, "E398", {"center": v(-150.2, -107) * mm, "radius": 1 * mm});
            skCircle(sketch, "E399", {"center": v(-89.5, -55.9) * mm, "radius": 1 * mm});
            skCircle(sketch, "E400", {"center": v(-87.5, -50.9) * mm, "radius": 1 * mm});
            skCircle(sketch, "E401", {"center": v(-131, -75) * mm, "radius": 1 * mm});
            skCircle(sketch, "E402", {"center": v(-120.8, -77) * mm, "radius": 1 * mm});
            skCircle(sketch, "E403", {"center": v(-52, -98) * mm, "radius": 1 * mm});
            skCircle(sketch, "E404", {"center": v(-50, -93) * mm, "radius": 1 * mm});
            skCircle(sketch, "E405", {"center": v(-34, -98) * mm, "radius": 1 * mm});
            skCircle(sketch, "E406", {"center": v(-32, -93) * mm, "radius": 1 * mm});
            skCircle(sketch, "E407", {"center": v(-16, -98) * mm, "radius": 1 * mm});
            skCircle(sketch, "E408", {"center": v(-14, -93) * mm, "radius": 1 * mm});
            skCircle(sketch, "E409", {"center": v(2, -98) * mm, "radius": 1 * mm});
            skCircle(sketch, "E410", {"center": v(4, -93) * mm, "radius": 1 * mm});
            skCircle(sketch, "E411", {"center": v(20, -98) * mm, "radius": 1 * mm});
            skCircle(sketch, "E412", {"center": v(22, -93) * mm, "radius": 1 * mm});
            skCircle(sketch, "E413", {"center": v(38, -98) * mm, "radius": 1 * mm});
            skCircle(sketch, "E414", {"center": v(40, -93) * mm, "radius": 1 * mm});
            skCircle(sketch, "E415", {"center": v(-88, -118) * mm, "radius": 1 * mm});
            skCircle(sketch, "E416", {"center": v(-86, -113) * mm, "radius": 1 * mm});
            skCircle(sketch, "E417", {"center": v(-11.5, -42.9) * mm, "radius": 1 * mm});
            skCircle(sketch, "E418", {"center": v(-13.5, -47.9) * mm, "radius": 1 * mm});
            skCircle(sketch, "E419", {"center": v(18.5, -42.9) * mm, "radius": 1 * mm});
            skCircle(sketch, "E420", {"center": v(16.5, -47.9) * mm, "radius": 1 * mm});
            skCircle(sketch, "E421", {"center": v(-150, -60) * mm, "radius": 1 * mm});
            skCircle(sketch, "E422", {"center": v(-139.8, -62) * mm, "radius": 1 * mm});
            skCircle(sketch, "E423", {"center": v(-138, -20.46) * mm, "radius": 0.76 * mm});
            skCircle(sketch, "E424", {"center": v(-138, -23) * mm, "radius": 0.76 * mm});
            skCircle(sketch, "E425", {"center": v(-138, -98.46) * mm, "radius": 0.76 * mm});
            skCircle(sketch, "E426", {"center": v(-138, -101) * mm, "radius": 0.76 * mm});
            skCircle(sketch, "E427", {"center": v(-127, -108.46) * mm, "radius": 0.76 * mm});
            skCircle(sketch, "E428", {"center": v(-127, -111) * mm, "radius": 0.76 * mm});
            skCircle(sketch, "E429", {"center": v(-121, -108.46) * mm, "radius": 0.76 * mm});
            skCircle(sketch, "E430", {"center": v(-121, -111) * mm, "radius": 0.76 * mm});
            skCircle(sketch, "E431", {"center": v(-138, -52.46) * mm, "radius": 0.76 * mm});
            skCircle(sketch, "E432", {"center": v(-138, -55) * mm, "radius": 0.76 * mm});
            skCircle(sketch, "E433", {"center": v(-120.86, 131.12) * mm, "radius": 0.76 * mm});
            skCircle(sketch, "E434", {"center": v(-123.4, 128.58) * mm, "radius": 0.76 * mm});
            skCircle(sketch, "E435", {"center": v(-120.86, 128.58) * mm, "radius": 0.76 * mm});
            skCircle(sketch, "E436", {"center": v(-123.4, 126.04) * mm, "radius": 0.76 * mm});
            skCircle(sketch, "E437", {"center": v(-120.86, 126.04) * mm, "radius": 0.76 * mm});
            skCircle(sketch, "E438", {"center": v(-123.4, 123.5) * mm, "radius": 0.76 * mm});
            skCircle(sketch, "E439", {"center": v(-120.86, 123.5) * mm, "radius": 0.76 * mm});
            skCircle(sketch, "E440", {"center": v(-123.4, 120.96) * mm, "radius": 0.76 * mm});
            skCircle(sketch, "E441", {"center": v(-120.86, 120.96) * mm, "radius": 0.76 * mm});
            skCircle(sketch, "E442", {"center": v(-123.4, 118.42) * mm, "radius": 0.76 * mm});
            skCircle(sketch, "E443", {"center": v(-120.86, 118.42) * mm, "radius": 0.76 * mm});
            skCircle(sketch, "E444", {"center": v(-123.4, 115.88) * mm, "radius": 0.76 * mm});
            skCircle(sketch, "E445", {"center": v(-120.86, 115.88) * mm, "radius": 0.76 * mm});
            skCircle(sketch, "E446", {"center": v(-123.4, 113.34) * mm, "radius": 0.76 * mm});
            skCircle(sketch, "E447", {"center": v(-120.86, 113.34) * mm, "radius": 0.76 * mm});
            skCircle(sketch, "E448", {"center": v(-123.4, 110.8) * mm, "radius": 0.76 * mm});
            skCircle(sketch, "E449", {"center": v(-120.86, 110.8) * mm, "radius": 0.76 * mm});
            skCircle(sketch, "E450", {"center": v(-123.4, 108.26) * mm, "radius": 0.76 * mm});
            skCircle(sketch, "E451", {"center": v(-120.86, 108.26) * mm, "radius": 0.76 * mm});
            skCircle(sketch, "E452", {"center": v(-123.4, 105.72) * mm, "radius": 0.76 * mm});
            skCircle(sketch, "E453", {"center": v(-120.86, 105.72) * mm, "radius": 0.76 * mm});
            skCircle(sketch, "E454", {"center": v(-123.4, 103.18) * mm, "radius": 0.76 * mm});
            skCircle(sketch, "E455", {"center": v(-120.86, 103.18) * mm, "radius": 0.76 * mm});
            skCircle(sketch, "E456", {"center": v(-123.4, 100.64) * mm, "radius": 0.76 * mm});
            skCircle(sketch, "E457", {"center": v(-120.86, 100.64) * mm, "radius": 0.76 * mm});
            skCircle(sketch, "E458", {"center": v(-123.4, 98.1) * mm, "radius": 0.76 * mm});
            skCircle(sketch, "E459", {"center": v(-120.86, 98.1) * mm, "radius": 0.76 * mm});
            skCircle(sketch, "E460", {"center": v(-123.4, 95.56) * mm, "radius": 0.76 * mm});
            skCircle(sketch, "E461", {"center": v(-120.86, 95.56) * mm, "radius": 0.76 * mm});
            skCircle(sketch, "E462", {"center": v(-123.4, 93.02) * mm, "radius": 0.76 * mm});
            skCircle(sketch, "E463", {"center": v(-120.86, 93.02) * mm, "radius": 0.76 * mm});
            skCircle(sketch, "E464", {"center": v(-123.4, 90.48) * mm, "radius": 0.76 * mm});
            skCircle(sketch, "E465", {"center": v(-120.86, 90.48) * mm, "radius": 0.76 * mm});
            skCircle(sketch, "E466", {"center": v(-123.4, 87.94) * mm, "radius": 0.76 * mm});
            skCircle(sketch, "E467", {"center": v(-120.86, 87.94) * mm, "radius": 0.76 * mm});
            skCircle(sketch, "E468", {"center": v(-123.4, 85.4) * mm, "radius": 0.76 * mm});
            skCircle(sketch, "E469", {"center": v(-120.86, 85.4) * mm, "radius": 0.76 * mm});
            skCircle(sketch, "E470", {"center": v(-123.4, 82.86) * mm, "radius": 0.76 * mm});
            skCircle(sketch, "E471", {"center": v(-120.86, 82.86) * mm, "radius": 0.76 * mm});
            skCircle(sketch, "E472", {"center": v(-11.96, 131.12) * mm, "radius": 0.76 * mm});
            skCircle(sketch, "E473", {"center": v(-14.5, 128.58) * mm, "radius": 0.76 * mm});
            skCircle(sketch, "E474", {"center": v(-11.96, 128.58) * mm, "radius": 0.76 * mm});
            skCircle(sketch, "E475", {"center": v(-14.5, 126.04) * mm, "radius": 0.76 * mm});
            skCircle(sketch, "E476", {"center": v(-11.96, 126.04) * mm, "radius": 0.76 * mm});
            skCircle(sketch, "E477", {"center": v(-14.5, 123.5) * mm, "radius": 0.76 * mm});
            skCircle(sketch, "E478", {"center": v(-11.96, 123.5) * mm, "radius": 0.76 * mm});
            skCircle(sketch, "E479", {"center": v(-14.5, 120.96) * mm, "radius": 0.76 * mm});
            skCircle(sketch, "E480", {"center": v(-11.96, 120.96) * mm, "radius": 0.76 * mm});
            skCircle(sketch, "E481", {"center": v(-14.5, 118.42) * mm, "radius": 0.76 * mm});
            skCircle(sketch, "E482", {"center": v(-11.96, 118.42) * mm, "radius": 0.76 * mm});
            skCircle(sketch, "E483", {"center": v(-14.5, 115.88) * mm, "radius": 0.76 * mm});
            skCircle(sketch, "E484", {"center": v(-11.96, 115.88) * mm, "radius": 0.76 * mm});
            skCircle(sketch, "E485", {"center": v(-14.5, 113.34) * mm, "radius": 0.76 * mm});
            skCircle(sketch, "E486", {"center": v(-11.96, 113.34) * mm, "radius": 0.76 * mm});
            skCircle(sketch, "E487", {"center": v(-14.5, 110.8) * mm, "radius": 0.76 * mm});
            skCircle(sketch, "E488", {"center": v(-11.96, 110.8) * mm, "radius": 0.76 * mm});
            skCircle(sketch, "E489", {"center": v(-14.5, 108.26) * mm, "radius": 0.76 * mm});
            skCircle(sketch, "E490", {"center": v(-11.96, 108.26) * mm, "radius": 0.76 * mm});
            skCircle(sketch, "E491", {"center": v(-14.5, 105.72) * mm, "radius": 0.76 * mm});
            skCircle(sketch, "E492", {"center": v(-11.96, 105.72) * mm, "radius": 0.76 * mm});
            skCircle(sketch, "E493", {"center": v(-14.5, 103.18) * mm, "radius": 0.76 * mm});
            skCircle(sketch, "E494", {"center": v(-11.96, 103.18) * mm, "radius": 0.76 * mm});
            skCircle(sketch, "E495", {"center": v(-14.5, 100.64) * mm, "radius": 0.76 * mm});
            skCircle(sketch, "E496", {"center": v(-11.96, 100.64) * mm, "radius": 0.76 * mm});
            skCircle(sketch, "E497", {"center": v(-14.5, 98.1) * mm, "radius": 0.76 * mm});
            skCircle(sketch, "E498", {"center": v(-11.96, 98.1) * mm, "radius": 0.76 * mm});
            skCircle(sketch, "E499", {"center": v(-14.5, 95.56) * mm, "radius": 0.76 * mm});
            skCircle(sketch, "E500", {"center": v(-11.96, 95.56) * mm, "radius": 0.76 * mm});
            skCircle(sketch, "E501", {"center": v(-14.5, 93.02) * mm, "radius": 0.76 * mm});
            skCircle(sketch, "E502", {"center": v(-11.96, 93.02) * mm, "radius": 0.76 * mm});
            skCircle(sketch, "E503", {"center": v(-14.5, 90.48) * mm, "radius": 0.76 * mm});
            skCircle(sketch, "E504", {"center": v(-11.96, 90.48) * mm, "radius": 0.76 * mm});
            skCircle(sketch, "E505", {"center": v(-14.5, 87.94) * mm, "radius": 0.76 * mm});
            skCircle(sketch, "E506", {"center": v(-11.96, 87.94) * mm, "radius": 0.76 * mm});
            skCircle(sketch, "E507", {"center": v(-14.5, 85.4) * mm, "radius": 0.76 * mm});
            skCircle(sketch, "E508", {"center": v(-11.96, 85.4) * mm, "radius": 0.76 * mm});
            skCircle(sketch, "E509", {"center": v(-14.5, 82.86) * mm, "radius": 0.76 * mm});
            skCircle(sketch, "E510", {"center": v(-11.96, 82.86) * mm, "radius": 0.76 * mm});
            skCircle(sketch, "E511", {"center": v(12.24, 131.12) * mm, "radius": 0.76 * mm});
            skCircle(sketch, "E512", {"center": v(9.7, 128.58) * mm, "radius": 0.76 * mm});
            skCircle(sketch, "E513", {"center": v(12.24, 128.58) * mm, "radius": 0.76 * mm});
            skCircle(sketch, "E514", {"center": v(9.7, 126.04) * mm, "radius": 0.76 * mm});
            skCircle(sketch, "E515", {"center": v(12.24, 126.04) * mm, "radius": 0.76 * mm});
            skCircle(sketch, "E516", {"center": v(9.7, 123.5) * mm, "radius": 0.76 * mm});
            skCircle(sketch, "E517", {"center": v(12.24, 123.5) * mm, "radius": 0.76 * mm});
            skCircle(sketch, "E518", {"center": v(9.7, 120.96) * mm, "radius": 0.76 * mm});
            skCircle(sketch, "E519", {"center": v(12.24, 120.96) * mm, "radius": 0.76 * mm});
            skCircle(sketch, "E520", {"center": v(9.7, 118.42) * mm, "radius": 0.76 * mm});
            skCircle(sketch, "E521", {"center": v(12.24, 118.42) * mm, "radius": 0.76 * mm});
            skCircle(sketch, "E522", {"center": v(9.7, 115.88) * mm, "radius": 0.76 * mm});
            skCircle(sketch, "E523", {"center": v(12.24, 115.88) * mm, "radius": 0.76 * mm});
            skCircle(sketch, "E524", {"center": v(9.7, 113.34) * mm, "radius": 0.76 * mm});
            skCircle(sketch, "E525", {"center": v(12.24, 113.34) * mm, "radius": 0.76 * mm});
            skCircle(sketch, "E526", {"center": v(9.7, 110.8) * mm, "radius": 0.76 * mm});
            skCircle(sketch, "E527", {"center": v(12.24, 110.8) * mm, "radius": 0.76 * mm});
            skCircle(sketch, "E528", {"center": v(9.7, 108.26) * mm, "radius": 0.76 * mm});
            skCircle(sketch, "E529", {"center": v(12.24, 108.26) * mm, "radius": 0.76 * mm});
            skCircle(sketch, "E530", {"center": v(9.7, 105.72) * mm, "radius": 0.76 * mm});
            skCircle(sketch, "E531", {"center": v(12.24, 105.72) * mm, "radius": 0.76 * mm});
            skCircle(sketch, "E532", {"center": v(9.7, 103.18) * mm, "radius": 0.76 * mm});
            skCircle(sketch, "E533", {"center": v(12.24, 103.18) * mm, "radius": 0.76 * mm});
            skCircle(sketch, "E534", {"center": v(9.7, 100.64) * mm, "radius": 0.76 * mm});
            skCircle(sketch, "E535", {"center": v(12.24, 100.64) * mm, "radius": 0.76 * mm});
            skCircle(sketch, "E536", {"center": v(9.7, 98.1) * mm, "radius": 0.76 * mm});
            skCircle(sketch, "E537", {"center": v(12.24, 98.1) * mm, "radius": 0.76 * mm});
            skCircle(sketch, "E538", {"center": v(9.7, 95.56) * mm, "radius": 0.76 * mm});
            skCircle(sketch, "E539", {"center": v(12.24, 95.56) * mm, "radius": 0.76 * mm});
            skCircle(sketch, "E540", {"center": v(9.7, 93.02) * mm, "radius": 0.76 * mm});
            skCircle(sketch, "E541", {"center": v(12.24, 93.02) * mm, "radius": 0.76 * mm});
            skCircle(sketch, "E542", {"center": v(9.7, 90.48) * mm, "radius": 0.76 * mm});
            skCircle(sketch, "E543", {"center": v(12.24, 90.48) * mm, "radius": 0.76 * mm});
            skCircle(sketch, "E544", {"center": v(9.7, 87.94) * mm, "radius": 0.76 * mm});
            skCircle(sketch, "E545", {"center": v(12.24, 87.94) * mm, "radius": 0.76 * mm});
            skCircle(sketch, "E546", {"center": v(9.7, 85.4) * mm, "radius": 0.76 * mm});
            skCircle(sketch, "E547", {"center": v(12.24, 85.4) * mm, "radius": 0.76 * mm});
            skCircle(sketch, "E548", {"center": v(9.7, 82.86) * mm, "radius": 0.76 * mm});
            skCircle(sketch, "E549", {"center": v(12.24, 82.86) * mm, "radius": 0.76 * mm});
            skCircle(sketch, "E550", {"center": v(24.34, 131.12) * mm, "radius": 0.76 * mm});
            skCircle(sketch, "E551", {"center": v(21.8, 128.58) * mm, "radius": 0.76 * mm});
            skCircle(sketch, "E552", {"center": v(24.34, 128.58) * mm, "radius": 0.76 * mm});
            skCircle(sketch, "E553", {"center": v(21.8, 126.04) * mm, "radius": 0.76 * mm});
            skCircle(sketch, "E554", {"center": v(24.34, 126.04) * mm, "radius": 0.76 * mm});
            skCircle(sketch, "E555", {"center": v(21.8, 123.5) * mm, "radius": 0.76 * mm});
            skCircle(sketch, "E556", {"center": v(24.34, 123.5) * mm, "radius": 0.76 * mm});
            skCircle(sketch, "E557", {"center": v(21.8, 120.96) * mm, "radius": 0.76 * mm});
            skCircle(sketch, "E558", {"center": v(24.34, 120.96) * mm, "radius": 0.76 * mm});
            skCircle(sketch, "E559", {"center": v(21.8, 118.42) * mm, "radius": 0.76 * mm});
            skCircle(sketch, "E560", {"center": v(24.34, 118.42) * mm, "radius": 0.76 * mm});
            skCircle(sketch, "E561", {"center": v(21.8, 115.88) * mm, "radius": 0.76 * mm});
            skCircle(sketch, "E562", {"center": v(24.34, 115.88) * mm, "radius": 0.76 * mm});
            skCircle(sketch, "E563", {"center": v(21.8, 113.34) * mm, "radius": 0.76 * mm});
            skCircle(sketch, "E564", {"center": v(24.34, 113.34) * mm, "radius": 0.76 * mm});
            skCircle(sketch, "E565", {"center": v(21.8, 110.8) * mm, "radius": 0.76 * mm});
            skCircle(sketch, "E566", {"center": v(24.34, 110.8) * mm, "radius": 0.76 * mm});
            skCircle(sketch, "E567", {"center": v(21.8, 108.26) * mm, "radius": 0.76 * mm});
            skCircle(sketch, "E568", {"center": v(24.34, 108.26) * mm, "radius": 0.76 * mm});
            skCircle(sketch, "E569", {"center": v(21.8, 105.72) * mm, "radius": 0.76 * mm});
            skCircle(sketch, "E570", {"center": v(24.34, 105.72) * mm, "radius": 0.76 * mm});
            skCircle(sketch, "E571", {"center": v(21.8, 103.18) * mm, "radius": 0.76 * mm});
            skCircle(sketch, "E572", {"center": v(24.34, 103.18) * mm, "radius": 0.76 * mm});
            skCircle(sketch, "E573", {"center": v(21.8, 100.64) * mm, "radius": 0.76 * mm});
            skCircle(sketch, "E574", {"center": v(24.34, 100.64) * mm, "radius": 0.76 * mm});
            skCircle(sketch, "E575", {"center": v(21.8, 98.1) * mm, "radius": 0.76 * mm});
            skCircle(sketch, "E576", {"center": v(24.34, 98.1) * mm, "radius": 0.76 * mm});
            skCircle(sketch, "E577", {"center": v(21.8, 95.56) * mm, "radius": 0.76 * mm});
            skCircle(sketch, "E578", {"center": v(24.34, 95.56) * mm, "radius": 0.76 * mm});
            skCircle(sketch, "E579", {"center": v(21.8, 93.02) * mm, "radius": 0.76 * mm});
            skCircle(sketch, "E580", {"center": v(24.34, 93.02) * mm, "radius": 0.76 * mm});
            skCircle(sketch, "E581", {"center": v(21.8, 90.48) * mm, "radius": 0.76 * mm});
            skCircle(sketch, "E582", {"center": v(24.34, 90.48) * mm, "radius": 0.76 * mm});
            skCircle(sketch, "E583", {"center": v(21.8, 87.94) * mm, "radius": 0.76 * mm});
            skCircle(sketch, "E584", {"center": v(24.34, 87.94) * mm, "radius": 0.76 * mm});
            skCircle(sketch, "E585", {"center": v(21.8, 85.4) * mm, "radius": 0.76 * mm});
            skCircle(sketch, "E586", {"center": v(24.34, 85.4) * mm, "radius": 0.76 * mm});
            skCircle(sketch, "E587", {"center": v(21.8, 82.86) * mm, "radius": 0.76 * mm});
            skCircle(sketch, "E588", {"center": v(24.34, 82.86) * mm, "radius": 0.76 * mm});
            skCircle(sketch, "E589", {"center": v(36.44, 131.12) * mm, "radius": 0.76 * mm});
            skCircle(sketch, "E590", {"center": v(33.9, 128.58) * mm, "radius": 0.76 * mm});
            skCircle(sketch, "E591", {"center": v(36.44, 128.58) * mm, "radius": 0.76 * mm});
            skCircle(sketch, "E592", {"center": v(33.9, 126.04) * mm, "radius": 0.76 * mm});
            skCircle(sketch, "E593", {"center": v(36.44, 126.04) * mm, "radius": 0.76 * mm});
            skCircle(sketch, "E594", {"center": v(33.9, 123.5) * mm, "radius": 0.76 * mm});
            skCircle(sketch, "E595", {"center": v(36.44, 123.5) * mm, "radius": 0.76 * mm});
            skCircle(sketch, "E596", {"center": v(33.9, 120.96) * mm, "radius": 0.76 * mm});
            skCircle(sketch, "E597", {"center": v(36.44, 120.96) * mm, "radius": 0.76 * mm});
            skCircle(sketch, "E598", {"center": v(33.9, 118.42) * mm, "radius": 0.76 * mm});
            skCircle(sketch, "E599", {"center": v(36.44, 118.42) * mm, "radius": 0.76 * mm});
            skCircle(sketch, "E600", {"center": v(33.9, 115.88) * mm, "radius": 0.76 * mm});
            skCircle(sketch, "E601", {"center": v(36.44, 115.88) * mm, "radius": 0.76 * mm});
            skCircle(sketch, "E602", {"center": v(33.9, 113.34) * mm, "radius": 0.76 * mm});
            skCircle(sketch, "E603", {"center": v(36.44, 113.34) * mm, "radius": 0.76 * mm});
            skCircle(sketch, "E604", {"center": v(33.9, 110.8) * mm, "radius": 0.76 * mm});
            skCircle(sketch, "E605", {"center": v(36.44, 110.8) * mm, "radius": 0.76 * mm});
            skCircle(sketch, "E606", {"center": v(33.9, 108.26) * mm, "radius": 0.76 * mm});
            skCircle(sketch, "E607", {"center": v(36.44, 108.26) * mm, "radius": 0.76 * mm});
            skCircle(sketch, "E608", {"center": v(33.9, 105.72) * mm, "radius": 0.76 * mm});
            skCircle(sketch, "E609", {"center": v(36.44, 105.72) * mm, "radius": 0.76 * mm});
            skCircle(sketch, "E610", {"center": v(33.9, 103.18) * mm, "radius": 0.76 * mm});
            skCircle(sketch, "E611", {"center": v(36.44, 103.18) * mm, "radius": 0.76 * mm});
            skCircle(sketch, "E612", {"center": v(33.9, 100.64) * mm, "radius": 0.76 * mm});
            skCircle(sketch, "E613", {"center": v(36.44, 100.64) * mm, "radius": 0.76 * mm});
            skCircle(sketch, "E614", {"center": v(33.9, 98.1) * mm, "radius": 0.76 * mm});
            skCircle(sketch, "E615", {"center": v(36.44, 98.1) * mm, "radius": 0.76 * mm});
            skCircle(sketch, "E616", {"center": v(33.9, 95.56) * mm, "radius": 0.76 * mm});
            skCircle(sketch, "E617", {"center": v(36.44, 95.56) * mm, "radius": 0.76 * mm});
            skCircle(sketch, "E618", {"center": v(33.9, 93.02) * mm, "radius": 0.76 * mm});
            skCircle(sketch, "E619", {"center": v(36.44, 93.02) * mm, "radius": 0.76 * mm});
            skCircle(sketch, "E620", {"center": v(33.9, 90.48) * mm, "radius": 0.76 * mm});
            skCircle(sketch, "E621", {"center": v(36.44, 90.48) * mm, "radius": 0.76 * mm});
            skCircle(sketch, "E622", {"center": v(33.9, 87.94) * mm, "radius": 0.76 * mm});
            skCircle(sketch, "E623", {"center": v(36.44, 87.94) * mm, "radius": 0.76 * mm});
            skCircle(sketch, "E624", {"center": v(33.9, 85.4) * mm, "radius": 0.76 * mm});
            skCircle(sketch, "E625", {"center": v(36.44, 85.4) * mm, "radius": 0.76 * mm});
            skCircle(sketch, "E626", {"center": v(33.9, 82.86) * mm, "radius": 0.76 * mm});
            skCircle(sketch, "E627", {"center": v(36.44, 82.86) * mm, "radius": 0.76 * mm});
            skCircle(sketch, "E628", {"center": v(48.54, 131.12) * mm, "radius": 0.76 * mm});
            skCircle(sketch, "E629", {"center": v(46, 128.58) * mm, "radius": 0.76 * mm});
            skCircle(sketch, "E630", {"center": v(48.54, 128.58) * mm, "radius": 0.76 * mm});
            skCircle(sketch, "E631", {"center": v(46, 126.04) * mm, "radius": 0.76 * mm});
            skCircle(sketch, "E632", {"center": v(48.54, 126.04) * mm, "radius": 0.76 * mm});
            skCircle(sketch, "E633", {"center": v(46, 123.5) * mm, "radius": 0.76 * mm});
            skCircle(sketch, "E634", {"center": v(48.54, 123.5) * mm, "radius": 0.76 * mm});
            skCircle(sketch, "E635", {"center": v(46, 120.96) * mm, "radius": 0.76 * mm});
            skCircle(sketch, "E636", {"center": v(48.54, 120.96) * mm, "radius": 0.76 * mm});
            skCircle(sketch, "E637", {"center": v(46, 118.42) * mm, "radius": 0.76 * mm});
            skCircle(sketch, "E638", {"center": v(48.54, 118.42) * mm, "radius": 0.76 * mm});
            skCircle(sketch, "E639", {"center": v(46, 115.88) * mm, "radius": 0.76 * mm});
            skCircle(sketch, "E640", {"center": v(48.54, 115.88) * mm, "radius": 0.76 * mm});
            skCircle(sketch, "E641", {"center": v(46, 113.34) * mm, "radius": 0.76 * mm});
            skCircle(sketch, "E642", {"center": v(48.54, 113.34) * mm, "radius": 0.76 * mm});
            skCircle(sketch, "E643", {"center": v(46, 110.8) * mm, "radius": 0.76 * mm});
            skCircle(sketch, "E644", {"center": v(48.54, 110.8) * mm, "radius": 0.76 * mm});
            skCircle(sketch, "E645", {"center": v(46, 108.26) * mm, "radius": 0.76 * mm});
            skCircle(sketch, "E646", {"center": v(48.54, 108.26) * mm, "radius": 0.76 * mm});
            skCircle(sketch, "E647", {"center": v(46, 105.72) * mm, "radius": 0.76 * mm});
            skCircle(sketch, "E648", {"center": v(48.54, 105.72) * mm, "radius": 0.76 * mm});
            skCircle(sketch, "E649", {"center": v(46, 103.18) * mm, "radius": 0.76 * mm});
            skCircle(sketch, "E650", {"center": v(48.54, 103.18) * mm, "radius": 0.76 * mm});
            skCircle(sketch, "E651", {"center": v(46, 100.64) * mm, "radius": 0.76 * mm});
            skCircle(sketch, "E652", {"center": v(48.54, 100.64) * mm, "radius": 0.76 * mm});
            skCircle(sketch, "E653", {"center": v(46, 98.1) * mm, "radius": 0.76 * mm});
            skCircle(sketch, "E654", {"center": v(48.54, 98.1) * mm, "radius": 0.76 * mm});
            skCircle(sketch, "E655", {"center": v(46, 95.56) * mm, "radius": 0.76 * mm});
            skCircle(sketch, "E656", {"center": v(48.54, 95.56) * mm, "radius": 0.76 * mm});
            skCircle(sketch, "E657", {"center": v(46, 93.02) * mm, "radius": 0.76 * mm});
            skCircle(sketch, "E658", {"center": v(48.54, 93.02) * mm, "radius": 0.76 * mm});
            skCircle(sketch, "E659", {"center": v(46, 90.48) * mm, "radius": 0.76 * mm});
            skCircle(sketch, "E660", {"center": v(48.54, 90.48) * mm, "radius": 0.76 * mm});
            skCircle(sketch, "E661", {"center": v(46, 87.94) * mm, "radius": 0.76 * mm});
            skCircle(sketch, "E662", {"center": v(48.54, 87.94) * mm, "radius": 0.76 * mm});
            skCircle(sketch, "E663", {"center": v(46, 85.4) * mm, "radius": 0.76 * mm});
            skCircle(sketch, "E664", {"center": v(48.54, 85.4) * mm, "radius": 0.76 * mm});
            skCircle(sketch, "E665", {"center": v(46, 82.86) * mm, "radius": 0.76 * mm});
            skCircle(sketch, "E666", {"center": v(48.54, 82.86) * mm, "radius": 0.76 * mm});
            skCircle(sketch, "E667", {"center": v(60.64, 131.12) * mm, "radius": 0.76 * mm});
            skCircle(sketch, "E668", {"center": v(58.1, 128.58) * mm, "radius": 0.76 * mm});
            skCircle(sketch, "E669", {"center": v(60.64, 128.58) * mm, "radius": 0.76 * mm});
            skCircle(sketch, "E670", {"center": v(58.1, 126.04) * mm, "radius": 0.76 * mm});
            skCircle(sketch, "E671", {"center": v(60.64, 126.04) * mm, "radius": 0.76 * mm});
            skCircle(sketch, "E672", {"center": v(58.1, 123.5) * mm, "radius": 0.76 * mm});
            skCircle(sketch, "E673", {"center": v(60.64, 123.5) * mm, "radius": 0.76 * mm});
            skCircle(sketch, "E674", {"center": v(58.1, 120.96) * mm, "radius": 0.76 * mm});
            skCircle(sketch, "E675", {"center": v(60.64, 120.96) * mm, "radius": 0.76 * mm});
            skCircle(sketch, "E676", {"center": v(58.1, 118.42) * mm, "radius": 0.76 * mm});
            skCircle(sketch, "E677", {"center": v(60.64, 118.42) * mm, "radius": 0.76 * mm});
            skCircle(sketch, "E678", {"center": v(58.1, 115.88) * mm, "radius": 0.76 * mm});
            skCircle(sketch, "E679", {"center": v(60.64, 115.88) * mm, "radius": 0.76 * mm});
            skCircle(sketch, "E680", {"center": v(58.1, 113.34) * mm, "radius": 0.76 * mm});
            skCircle(sketch, "E681", {"center": v(60.64, 113.34) * mm, "radius": 0.76 * mm});
            skCircle(sketch, "E682", {"center": v(58.1, 110.8) * mm, "radius": 0.76 * mm});
            skCircle(sketch, "E683", {"center": v(60.64, 110.8) * mm, "radius": 0.76 * mm});
            skCircle(sketch, "E684", {"center": v(58.1, 108.26) * mm, "radius": 0.76 * mm});
            skCircle(sketch, "E685", {"center": v(60.64, 108.26) * mm, "radius": 0.76 * mm});
            skCircle(sketch, "E686", {"center": v(58.1, 105.72) * mm, "radius": 0.76 * mm});
            skCircle(sketch, "E687", {"center": v(60.64, 105.72) * mm, "radius": 0.76 * mm});
            skCircle(sketch, "E688", {"center": v(58.1, 103.18) * mm, "radius": 0.76 * mm});
            skCircle(sketch, "E689", {"center": v(60.64, 103.18) * mm, "radius": 0.76 * mm});
            skCircle(sketch, "E690", {"center": v(58.1, 100.64) * mm, "radius": 0.76 * mm});
            skCircle(sketch, "E691", {"center": v(60.64, 100.64) * mm, "radius": 0.76 * mm});
            skCircle(sketch, "E692", {"center": v(58.1, 98.1) * mm, "radius": 0.76 * mm});
            skCircle(sketch, "E693", {"center": v(60.64, 98.1) * mm, "radius": 0.76 * mm});
            skCircle(sketch, "E694", {"center": v(58.1, 95.56) * mm, "radius": 0.76 * mm});
            skCircle(sketch, "E695", {"center": v(60.64, 95.56) * mm, "radius": 0.76 * mm});
            skCircle(sketch, "E696", {"center": v(58.1, 93.02) * mm, "radius": 0.76 * mm});
            skCircle(sketch, "E697", {"center": v(60.64, 93.02) * mm, "radius": 0.76 * mm});
            skCircle(sketch, "E698", {"center": v(58.1, 90.48) * mm, "radius": 0.76 * mm});
            skCircle(sketch, "E699", {"center": v(60.64, 90.48) * mm, "radius": 0.76 * mm});
            skCircle(sketch, "E700", {"center": v(58.1, 87.94) * mm, "radius": 0.76 * mm});
            skCircle(sketch, "E701", {"center": v(60.64, 87.94) * mm, "radius": 0.76 * mm});
            skCircle(sketch, "E702", {"center": v(58.1, 85.4) * mm, "radius": 0.76 * mm});
            skCircle(sketch, "E703", {"center": v(60.64, 85.4) * mm, "radius": 0.76 * mm});
            skCircle(sketch, "E704", {"center": v(58.1, 82.86) * mm, "radius": 0.76 * mm});
            skCircle(sketch, "E705", {"center": v(60.64, 82.86) * mm, "radius": 0.76 * mm});
            skCircle(sketch, "E706", {"center": v(72.74, 131.12) * mm, "radius": 0.76 * mm});
            skCircle(sketch, "E707", {"center": v(70.2, 128.58) * mm, "radius": 0.76 * mm});
            skCircle(sketch, "E708", {"center": v(72.74, 128.58) * mm, "radius": 0.76 * mm});
            skCircle(sketch, "E709", {"center": v(70.2, 126.04) * mm, "radius": 0.76 * mm});
            skCircle(sketch, "E710", {"center": v(72.74, 126.04) * mm, "radius": 0.76 * mm});
            skCircle(sketch, "E711", {"center": v(70.2, 123.5) * mm, "radius": 0.76 * mm});
            skCircle(sketch, "E712", {"center": v(72.74, 123.5) * mm, "radius": 0.76 * mm});
            skCircle(sketch, "E713", {"center": v(70.2, 120.96) * mm, "radius": 0.76 * mm});
            skCircle(sketch, "E714", {"center": v(72.74, 120.96) * mm, "radius": 0.76 * mm});
            skCircle(sketch, "E715", {"center": v(70.2, 118.42) * mm, "radius": 0.76 * mm});
            skCircle(sketch, "E716", {"center": v(72.74, 118.42) * mm, "radius": 0.76 * mm});
            skCircle(sketch, "E717", {"center": v(70.2, 115.88) * mm, "radius": 0.76 * mm});
            skCircle(sketch, "E718", {"center": v(72.74, 115.88) * mm, "radius": 0.76 * mm});
            skCircle(sketch, "E719", {"center": v(70.2, 113.34) * mm, "radius": 0.76 * mm});
            skCircle(sketch, "E720", {"center": v(72.74, 113.34) * mm, "radius": 0.76 * mm});
            skCircle(sketch, "E721", {"center": v(70.2, 110.8) * mm, "radius": 0.76 * mm});
            skCircle(sketch, "E722", {"center": v(72.74, 110.8) * mm, "radius": 0.76 * mm});
            skCircle(sketch, "E723", {"center": v(70.2, 108.26) * mm, "radius": 0.76 * mm});
            skCircle(sketch, "E724", {"center": v(72.74, 108.26) * mm, "radius": 0.76 * mm});
            skCircle(sketch, "E725", {"center": v(70.2, 105.72) * mm, "radius": 0.76 * mm});
            skCircle(sketch, "E726", {"center": v(72.74, 105.72) * mm, "radius": 0.76 * mm});
            skCircle(sketch, "E727", {"center": v(70.2, 103.18) * mm, "radius": 0.76 * mm});
            skCircle(sketch, "E728", {"center": v(72.74, 103.18) * mm, "radius": 0.76 * mm});
            skCircle(sketch, "E729", {"center": v(70.2, 100.64) * mm, "radius": 0.76 * mm});
            skCircle(sketch, "E730", {"center": v(72.74, 100.64) * mm, "radius": 0.76 * mm});
            skCircle(sketch, "E731", {"center": v(70.2, 98.1) * mm, "radius": 0.76 * mm});
            skCircle(sketch, "E732", {"center": v(72.74, 98.1) * mm, "radius": 0.76 * mm});
            skCircle(sketch, "E733", {"center": v(70.2, 95.56) * mm, "radius": 0.76 * mm});
            skCircle(sketch, "E734", {"center": v(72.74, 95.56) * mm, "radius": 0.76 * mm});
            skCircle(sketch, "E735", {"center": v(70.2, 93.02) * mm, "radius": 0.76 * mm});
            skCircle(sketch, "E736", {"center": v(72.74, 93.02) * mm, "radius": 0.76 * mm});
            skCircle(sketch, "E737", {"center": v(70.2, 90.48) * mm, "radius": 0.76 * mm});
            skCircle(sketch, "E738", {"center": v(72.74, 90.48) * mm, "radius": 0.76 * mm});
            skCircle(sketch, "E739", {"center": v(70.2, 87.94) * mm, "radius": 0.76 * mm});
            skCircle(sketch, "E740", {"center": v(72.74, 87.94) * mm, "radius": 0.76 * mm});
            skCircle(sketch, "E741", {"center": v(70.2, 85.4) * mm, "radius": 0.76 * mm});
            skCircle(sketch, "E742", {"center": v(72.74, 85.4) * mm, "radius": 0.76 * mm});
            skCircle(sketch, "E743", {"center": v(70.2, 82.86) * mm, "radius": 0.76 * mm});
            skCircle(sketch, "E744", {"center": v(72.74, 82.86) * mm, "radius": 0.76 * mm});
            skCircle(sketch, "E745", {"center": v(0.14, 131.12) * mm, "radius": 0.76 * mm});
            skCircle(sketch, "E746", {"center": v(-2.4, 128.58) * mm, "radius": 0.76 * mm});
            skCircle(sketch, "E747", {"center": v(0.14, 128.58) * mm, "radius": 0.76 * mm});
            skCircle(sketch, "E748", {"center": v(-2.4, 126.04) * mm, "radius": 0.76 * mm});
            skCircle(sketch, "E749", {"center": v(0.14, 126.04) * mm, "radius": 0.76 * mm});
            skCircle(sketch, "E750", {"center": v(-2.4, 123.5) * mm, "radius": 0.76 * mm});
            skCircle(sketch, "E751", {"center": v(0.14, 123.5) * mm, "radius": 0.76 * mm});
            skCircle(sketch, "E752", {"center": v(-2.4, 120.96) * mm, "radius": 0.76 * mm});
            skCircle(sketch, "E753", {"center": v(0.14, 120.96) * mm, "radius": 0.76 * mm});
            skCircle(sketch, "E754", {"center": v(-2.4, 118.42) * mm, "radius": 0.76 * mm});
            skCircle(sketch, "E755", {"center": v(0.14, 118.42) * mm, "radius": 0.76 * mm});
            skCircle(sketch, "E756", {"center": v(-2.4, 115.88) * mm, "radius": 0.76 * mm});
            skCircle(sketch, "E757", {"center": v(0.14, 115.88) * mm, "radius": 0.76 * mm});
            skCircle(sketch, "E758", {"center": v(-2.4, 113.34) * mm, "radius": 0.76 * mm});
            skCircle(sketch, "E759", {"center": v(0.14, 113.34) * mm, "radius": 0.76 * mm});
            skCircle(sketch, "E760", {"center": v(-2.4, 110.8) * mm, "radius": 0.76 * mm});
            skCircle(sketch, "E761", {"center": v(0.14, 110.8) * mm, "radius": 0.76 * mm});
            skCircle(sketch, "E762", {"center": v(-2.4, 108.26) * mm, "radius": 0.76 * mm});
            skCircle(sketch, "E763", {"center": v(0.14, 108.26) * mm, "radius": 0.76 * mm});
            skCircle(sketch, "E764", {"center": v(-2.4, 105.72) * mm, "radius": 0.76 * mm});
            skCircle(sketch, "E765", {"center": v(0.14, 105.72) * mm, "radius": 0.76 * mm});
            skCircle(sketch, "E766", {"center": v(-2.4, 103.18) * mm, "radius": 0.76 * mm});
            skCircle(sketch, "E767", {"center": v(0.14, 103.18) * mm, "radius": 0.76 * mm});
            skCircle(sketch, "E768", {"center": v(-2.4, 100.64) * mm, "radius": 0.76 * mm});
            skCircle(sketch, "E769", {"center": v(0.14, 100.64) * mm, "radius": 0.76 * mm});
            skCircle(sketch, "E770", {"center": v(-2.4, 98.1) * mm, "radius": 0.76 * mm});
            skCircle(sketch, "E771", {"center": v(0.14, 98.1) * mm, "radius": 0.76 * mm});
            skCircle(sketch, "E772", {"center": v(-2.4, 95.56) * mm, "radius": 0.76 * mm});
            skCircle(sketch, "E773", {"center": v(0.14, 95.56) * mm, "radius": 0.76 * mm});
            skCircle(sketch, "E774", {"center": v(-2.4, 93.02) * mm, "radius": 0.76 * mm});
            skCircle(sketch, "E775", {"center": v(0.14, 93.02) * mm, "radius": 0.76 * mm});
            skCircle(sketch, "E776", {"center": v(-2.4, 90.48) * mm, "radius": 0.76 * mm});
            skCircle(sketch, "E777", {"center": v(0.14, 90.48) * mm, "radius": 0.76 * mm});
            skCircle(sketch, "E778", {"center": v(-2.4, 87.94) * mm, "radius": 0.76 * mm});
            skCircle(sketch, "E779", {"center": v(0.14, 87.94) * mm, "radius": 0.76 * mm});
            skCircle(sketch, "E780", {"center": v(-2.4, 85.4) * mm, "radius": 0.76 * mm});
            skCircle(sketch, "E781", {"center": v(0.14, 85.4) * mm, "radius": 0.76 * mm});
            skCircle(sketch, "E782", {"center": v(-2.4, 82.86) * mm, "radius": 0.76 * mm});
            skCircle(sketch, "E783", {"center": v(0.14, 82.86) * mm, "radius": 0.76 * mm});
            skCircle(sketch, "E784", {"center": v(84.84, 131.12) * mm, "radius": 0.76 * mm});
            skCircle(sketch, "E785", {"center": v(82.3, 128.58) * mm, "radius": 0.76 * mm});
            skCircle(sketch, "E786", {"center": v(84.84, 128.58) * mm, "radius": 0.76 * mm});
            skCircle(sketch, "E787", {"center": v(82.3, 126.04) * mm, "radius": 0.76 * mm});
            skCircle(sketch, "E788", {"center": v(84.84, 126.04) * mm, "radius": 0.76 * mm});
            skCircle(sketch, "E789", {"center": v(82.3, 123.5) * mm, "radius": 0.76 * mm});
            skCircle(sketch, "E790", {"center": v(84.84, 123.5) * mm, "radius": 0.76 * mm});
            skCircle(sketch, "E791", {"center": v(82.3, 120.96) * mm, "radius": 0.76 * mm});
            skCircle(sketch, "E792", {"center": v(84.84, 120.96) * mm, "radius": 0.76 * mm});
            skCircle(sketch, "E793", {"center": v(82.3, 118.42) * mm, "radius": 0.76 * mm});
            skCircle(sketch, "E794", {"center": v(84.84, 118.42) * mm, "radius": 0.76 * mm});
            skCircle(sketch, "E795", {"center": v(82.3, 115.88) * mm, "radius": 0.76 * mm});
            skCircle(sketch, "E796", {"center": v(84.84, 115.88) * mm, "radius": 0.76 * mm});
            skCircle(sketch, "E797", {"center": v(82.3, 113.34) * mm, "radius": 0.76 * mm});
            skCircle(sketch, "E798", {"center": v(84.84, 113.34) * mm, "radius": 0.76 * mm});
            skCircle(sketch, "E799", {"center": v(82.3, 110.8) * mm, "radius": 0.76 * mm});
            skCircle(sketch, "E800", {"center": v(84.84, 110.8) * mm, "radius": 0.76 * mm});
            skCircle(sketch, "E801", {"center": v(82.3, 108.26) * mm, "radius": 0.76 * mm});
            skCircle(sketch, "E802", {"center": v(84.84, 108.26) * mm, "radius": 0.76 * mm});
            skCircle(sketch, "E803", {"center": v(82.3, 105.72) * mm, "radius": 0.76 * mm});
            skCircle(sketch, "E804", {"center": v(84.84, 105.72) * mm, "radius": 0.76 * mm});
            skCircle(sketch, "E805", {"center": v(82.3, 103.18) * mm, "radius": 0.76 * mm});
            skCircle(sketch, "E806", {"center": v(84.84, 103.18) * mm, "radius": 0.76 * mm});
            skCircle(sketch, "E807", {"center": v(82.3, 100.64) * mm, "radius": 0.76 * mm});
            skCircle(sketch, "E808", {"center": v(84.84, 100.64) * mm, "radius": 0.76 * mm});
            skCircle(sketch, "E809", {"center": v(82.3, 98.1) * mm, "radius": 0.76 * mm});
            skCircle(sketch, "E810", {"center": v(84.84, 98.1) * mm, "radius": 0.76 * mm});
            skCircle(sketch, "E811", {"center": v(82.3, 95.56) * mm, "radius": 0.76 * mm});
            skCircle(sketch, "E812", {"center": v(84.84, 95.56) * mm, "radius": 0.76 * mm});
            skCircle(sketch, "E813", {"center": v(82.3, 93.02) * mm, "radius": 0.76 * mm});
            skCircle(sketch, "E814", {"center": v(84.84, 93.02) * mm, "radius": 0.76 * mm});
            skCircle(sketch, "E815", {"center": v(82.3, 90.48) * mm, "radius": 0.76 * mm});
            skCircle(sketch, "E816", {"center": v(84.84, 90.48) * mm, "radius": 0.76 * mm});
            skCircle(sketch, "E817", {"center": v(82.3, 87.94) * mm, "radius": 0.76 * mm});
            skCircle(sketch, "E818", {"center": v(84.84, 87.94) * mm, "radius": 0.76 * mm});
            skCircle(sketch, "E819", {"center": v(82.3, 85.4) * mm, "radius": 0.76 * mm});
            skCircle(sketch, "E820", {"center": v(84.84, 85.4) * mm, "radius": 0.76 * mm});
            skCircle(sketch, "E821", {"center": v(82.3, 82.86) * mm, "radius": 0.76 * mm});
            skCircle(sketch, "E822", {"center": v(84.84, 82.86) * mm, "radius": 0.76 * mm});
            skCircle(sketch, "E823", {"center": v(96.94, 131.12) * mm, "radius": 0.76 * mm});
            skCircle(sketch, "E824", {"center": v(94.4, 128.58) * mm, "radius": 0.76 * mm});
            skCircle(sketch, "E825", {"center": v(96.94, 128.58) * mm, "radius": 0.76 * mm});
            skCircle(sketch, "E826", {"center": v(94.4, 126.04) * mm, "radius": 0.76 * mm});
            skCircle(sketch, "E827", {"center": v(96.94, 126.04) * mm, "radius": 0.76 * mm});
            skCircle(sketch, "E828", {"center": v(94.4, 123.5) * mm, "radius": 0.76 * mm});
            skCircle(sketch, "E829", {"center": v(96.94, 123.5) * mm, "radius": 0.76 * mm});
            skCircle(sketch, "E830", {"center": v(94.4, 120.96) * mm, "radius": 0.76 * mm});
            skCircle(sketch, "E831", {"center": v(96.94, 120.96) * mm, "radius": 0.76 * mm});
            skCircle(sketch, "E832", {"center": v(94.4, 118.42) * mm, "radius": 0.76 * mm});
            skCircle(sketch, "E833", {"center": v(96.94, 118.42) * mm, "radius": 0.76 * mm});
            skCircle(sketch, "E834", {"center": v(94.4, 115.88) * mm, "radius": 0.76 * mm});
            skCircle(sketch, "E835", {"center": v(96.94, 115.88) * mm, "radius": 0.76 * mm});
            skCircle(sketch, "E836", {"center": v(94.4, 113.34) * mm, "radius": 0.76 * mm});
            skCircle(sketch, "E837", {"center": v(96.94, 113.34) * mm, "radius": 0.76 * mm});
            skCircle(sketch, "E838", {"center": v(94.4, 110.8) * mm, "radius": 0.76 * mm});
            skCircle(sketch, "E839", {"center": v(96.94, 110.8) * mm, "radius": 0.76 * mm});
            skCircle(sketch, "E840", {"center": v(94.4, 108.26) * mm, "radius": 0.76 * mm});
            skCircle(sketch, "E841", {"center": v(96.94, 108.26) * mm, "radius": 0.76 * mm});
            skCircle(sketch, "E842", {"center": v(94.4, 105.72) * mm, "radius": 0.76 * mm});
            skCircle(sketch, "E843", {"center": v(96.94, 105.72) * mm, "radius": 0.76 * mm});
            skCircle(sketch, "E844", {"center": v(94.4, 103.18) * mm, "radius": 0.76 * mm});
            skCircle(sketch, "E845", {"center": v(96.94, 103.18) * mm, "radius": 0.76 * mm});
            skCircle(sketch, "E846", {"center": v(94.4, 100.64) * mm, "radius": 0.76 * mm});
            skCircle(sketch, "E847", {"center": v(96.94, 100.64) * mm, "radius": 0.76 * mm});
            skCircle(sketch, "E848", {"center": v(94.4, 98.1) * mm, "radius": 0.76 * mm});
            skCircle(sketch, "E849", {"center": v(96.94, 98.1) * mm, "radius": 0.76 * mm});
            skCircle(sketch, "E850", {"center": v(94.4, 95.56) * mm, "radius": 0.76 * mm});
            skCircle(sketch, "E851", {"center": v(96.94, 95.56) * mm, "radius": 0.76 * mm});
            skCircle(sketch, "E852", {"center": v(94.4, 93.02) * mm, "radius": 0.76 * mm});
            skCircle(sketch, "E853", {"center": v(96.94, 93.02) * mm, "radius": 0.76 * mm});
            skCircle(sketch, "E854", {"center": v(94.4, 90.48) * mm, "radius": 0.76 * mm});
            skCircle(sketch, "E855", {"center": v(96.94, 90.48) * mm, "radius": 0.76 * mm});
            skCircle(sketch, "E856", {"center": v(94.4, 87.94) * mm, "radius": 0.76 * mm});
            skCircle(sketch, "E857", {"center": v(96.94, 87.94) * mm, "radius": 0.76 * mm});
            skCircle(sketch, "E858", {"center": v(94.4, 85.4) * mm, "radius": 0.76 * mm});
            skCircle(sketch, "E859", {"center": v(96.94, 85.4) * mm, "radius": 0.76 * mm});
            skCircle(sketch, "E860", {"center": v(94.4, 82.86) * mm, "radius": 0.76 * mm});
            skCircle(sketch, "E861", {"center": v(96.94, 82.86) * mm, "radius": 0.76 * mm});
            skCircle(sketch, "E862", {"center": v(-96.66, 131.12) * mm, "radius": 0.76 * mm});
            skCircle(sketch, "E863", {"center": v(-99.2, 128.58) * mm, "radius": 0.76 * mm});
            skCircle(sketch, "E864", {"center": v(-96.66, 128.58) * mm, "radius": 0.76 * mm});
            skCircle(sketch, "E865", {"center": v(-99.2, 126.04) * mm, "radius": 0.76 * mm});
            skCircle(sketch, "E866", {"center": v(-96.66, 126.04) * mm, "radius": 0.76 * mm});
            skCircle(sketch, "E867", {"center": v(-99.2, 123.5) * mm, "radius": 0.76 * mm});
            skCircle(sketch, "E868", {"center": v(-96.66, 123.5) * mm, "radius": 0.76 * mm});
            skCircle(sketch, "E869", {"center": v(-99.2, 120.96) * mm, "radius": 0.76 * mm});
            skCircle(sketch, "E870", {"center": v(-96.66, 120.96) * mm, "radius": 0.76 * mm});
            skCircle(sketch, "E871", {"center": v(-99.2, 118.42) * mm, "radius": 0.76 * mm});
            skCircle(sketch, "E872", {"center": v(-96.66, 118.42) * mm, "radius": 0.76 * mm});
            skCircle(sketch, "E873", {"center": v(-99.2, 115.88) * mm, "radius": 0.76 * mm});
            skCircle(sketch, "E874", {"center": v(-96.66, 115.88) * mm, "radius": 0.76 * mm});
            skCircle(sketch, "E875", {"center": v(-99.2, 113.34) * mm, "radius": 0.76 * mm});
            skCircle(sketch, "E876", {"center": v(-96.66, 113.34) * mm, "radius": 0.76 * mm});
            skCircle(sketch, "E877", {"center": v(-99.2, 110.8) * mm, "radius": 0.76 * mm});
            skCircle(sketch, "E878", {"center": v(-96.66, 110.8) * mm, "radius": 0.76 * mm});
            skCircle(sketch, "E879", {"center": v(-99.2, 108.26) * mm, "radius": 0.76 * mm});
            skCircle(sketch, "E880", {"center": v(-96.66, 108.26) * mm, "radius": 0.76 * mm});
            skCircle(sketch, "E881", {"center": v(-99.2, 105.72) * mm, "radius": 0.76 * mm});
            skCircle(sketch, "E882", {"center": v(-96.66, 105.72) * mm, "radius": 0.76 * mm});
            skCircle(sketch, "E883", {"center": v(-99.2, 103.18) * mm, "radius": 0.76 * mm});
            skCircle(sketch, "E884", {"center": v(-96.66, 103.18) * mm, "radius": 0.76 * mm});
            skCircle(sketch, "E885", {"center": v(-99.2, 100.64) * mm, "radius": 0.76 * mm});
            skCircle(sketch, "E886", {"center": v(-96.66, 100.64) * mm, "radius": 0.76 * mm});
            skCircle(sketch, "E887", {"center": v(-99.2, 98.1) * mm, "radius": 0.76 * mm});
            skCircle(sketch, "E888", {"center": v(-96.66, 98.1) * mm, "radius": 0.76 * mm});
            skCircle(sketch, "E889", {"center": v(-99.2, 95.56) * mm, "radius": 0.76 * mm});
            skCircle(sketch, "E890", {"center": v(-96.66, 95.56) * mm, "radius": 0.76 * mm});
            skCircle(sketch, "E891", {"center": v(-99.2, 93.02) * mm, "radius": 0.76 * mm});
            skCircle(sketch, "E892", {"center": v(-96.66, 93.02) * mm, "radius": 0.76 * mm});
            skCircle(sketch, "E893", {"center": v(-99.2, 90.48) * mm, "radius": 0.76 * mm});
            skCircle(sketch, "E894", {"center": v(-96.66, 90.48) * mm, "radius": 0.76 * mm});
            skCircle(sketch, "E895", {"center": v(-99.2, 87.94) * mm, "radius": 0.76 * mm});
            skCircle(sketch, "E896", {"center": v(-96.66, 87.94) * mm, "radius": 0.76 * mm});
            skCircle(sketch, "E897", {"center": v(-99.2, 85.4) * mm, "radius": 0.76 * mm});
            skCircle(sketch, "E898", {"center": v(-96.66, 85.4) * mm, "radius": 0.76 * mm});
            skCircle(sketch, "E899", {"center": v(-99.2, 82.86) * mm, "radius": 0.76 * mm});
            skCircle(sketch, "E900", {"center": v(-96.66, 82.86) * mm, "radius": 0.76 * mm});
            skCircle(sketch, "E901", {"center": v(109.04, 131.12) * mm, "radius": 0.76 * mm});
            skCircle(sketch, "E902", {"center": v(106.5, 128.58) * mm, "radius": 0.76 * mm});
            skCircle(sketch, "E903", {"center": v(109.04, 128.58) * mm, "radius": 0.76 * mm});
            skCircle(sketch, "E904", {"center": v(106.5, 126.04) * mm, "radius": 0.76 * mm});
            skCircle(sketch, "E905", {"center": v(109.04, 126.04) * mm, "radius": 0.76 * mm});
            skCircle(sketch, "E906", {"center": v(106.5, 123.5) * mm, "radius": 0.76 * mm});
            skCircle(sketch, "E907", {"center": v(109.04, 123.5) * mm, "radius": 0.76 * mm});
            skCircle(sketch, "E908", {"center": v(106.5, 120.96) * mm, "radius": 0.76 * mm});
            skCircle(sketch, "E909", {"center": v(109.04, 120.96) * mm, "radius": 0.76 * mm});
            skCircle(sketch, "E910", {"center": v(106.5, 118.42) * mm, "radius": 0.76 * mm});
            skCircle(sketch, "E911", {"center": v(109.04, 118.42) * mm, "radius": 0.76 * mm});
            skCircle(sketch, "E912", {"center": v(106.5, 115.88) * mm, "radius": 0.76 * mm});
            skCircle(sketch, "E913", {"center": v(109.04, 115.88) * mm, "radius": 0.76 * mm});
            skCircle(sketch, "E914", {"center": v(106.5, 113.34) * mm, "radius": 0.76 * mm});
            skCircle(sketch, "E915", {"center": v(109.04, 113.34) * mm, "radius": 0.76 * mm});
            skCircle(sketch, "E916", {"center": v(106.5, 110.8) * mm, "radius": 0.76 * mm});
            skCircle(sketch, "E917", {"center": v(109.04, 110.8) * mm, "radius": 0.76 * mm});
            skCircle(sketch, "E918", {"center": v(106.5, 108.26) * mm, "radius": 0.76 * mm});
            skCircle(sketch, "E919", {"center": v(109.04, 108.26) * mm, "radius": 0.76 * mm});
            skCircle(sketch, "E920", {"center": v(106.5, 105.72) * mm, "radius": 0.76 * mm});
            skCircle(sketch, "E921", {"center": v(109.04, 105.72) * mm, "radius": 0.76 * mm});
            skCircle(sketch, "E922", {"center": v(106.5, 103.18) * mm, "radius": 0.76 * mm});
            skCircle(sketch, "E923", {"center": v(109.04, 103.18) * mm, "radius": 0.76 * mm});
            skCircle(sketch, "E924", {"center": v(106.5, 100.64) * mm, "radius": 0.76 * mm});
            skCircle(sketch, "E925", {"center": v(109.04, 100.64) * mm, "radius": 0.76 * mm});
            skCircle(sketch, "E926", {"center": v(106.5, 98.1) * mm, "radius": 0.76 * mm});
            skCircle(sketch, "E927", {"center": v(109.04, 98.1) * mm, "radius": 0.76 * mm});
            skCircle(sketch, "E928", {"center": v(106.5, 95.56) * mm, "radius": 0.76 * mm});
            skCircle(sketch, "E929", {"center": v(109.04, 95.56) * mm, "radius": 0.76 * mm});
            skCircle(sketch, "E930", {"center": v(106.5, 93.02) * mm, "radius": 0.76 * mm});
            skCircle(sketch, "E931", {"center": v(109.04, 93.02) * mm, "radius": 0.76 * mm});
            skCircle(sketch, "E932", {"center": v(106.5, 90.48) * mm, "radius": 0.76 * mm});
            skCircle(sketch, "E933", {"center": v(109.04, 90.48) * mm, "radius": 0.76 * mm});
            skCircle(sketch, "E934", {"center": v(106.5, 87.94) * mm, "radius": 0.76 * mm});
            skCircle(sketch, "E935", {"center": v(109.04, 87.94) * mm, "radius": 0.76 * mm});
            skCircle(sketch, "E936", {"center": v(106.5, 85.4) * mm, "radius": 0.76 * mm});
            skCircle(sketch, "E937", {"center": v(109.04, 85.4) * mm, "radius": 0.76 * mm});
            skCircle(sketch, "E938", {"center": v(106.5, 82.86) * mm, "radius": 0.76 * mm});
            skCircle(sketch, "E939", {"center": v(109.04, 82.86) * mm, "radius": 0.76 * mm});
            skCircle(sketch, "E940", {"center": v(121.14, 131.12) * mm, "radius": 0.76 * mm});
            skCircle(sketch, "E941", {"center": v(118.6, 128.58) * mm, "radius": 0.76 * mm});
            skCircle(sketch, "E942", {"center": v(121.14, 128.58) * mm, "radius": 0.76 * mm});
            skCircle(sketch, "E943", {"center": v(118.6, 126.04) * mm, "radius": 0.76 * mm});
            skCircle(sketch, "E944", {"center": v(121.14, 126.04) * mm, "radius": 0.76 * mm});
            skCircle(sketch, "E945", {"center": v(118.6, 123.5) * mm, "radius": 0.76 * mm});
            skCircle(sketch, "E946", {"center": v(121.14, 123.5) * mm, "radius": 0.76 * mm});
            skCircle(sketch, "E947", {"center": v(118.6, 120.96) * mm, "radius": 0.76 * mm});
            skCircle(sketch, "E948", {"center": v(121.14, 120.96) * mm, "radius": 0.76 * mm});
            skCircle(sketch, "E949", {"center": v(118.6, 118.42) * mm, "radius": 0.76 * mm});
            skCircle(sketch, "E950", {"center": v(121.14, 118.42) * mm, "radius": 0.76 * mm});
            skCircle(sketch, "E951", {"center": v(118.6, 115.88) * mm, "radius": 0.76 * mm});
            skCircle(sketch, "E952", {"center": v(121.14, 115.88) * mm, "radius": 0.76 * mm});
            skCircle(sketch, "E953", {"center": v(118.6, 113.34) * mm, "radius": 0.76 * mm});
            skCircle(sketch, "E954", {"center": v(121.14, 113.34) * mm, "radius": 0.76 * mm});
            skCircle(sketch, "E955", {"center": v(118.6, 110.8) * mm, "radius": 0.76 * mm});
            skCircle(sketch, "E956", {"center": v(121.14, 110.8) * mm, "radius": 0.76 * mm});
            skCircle(sketch, "E957", {"center": v(118.6, 108.26) * mm, "radius": 0.76 * mm});
            skCircle(sketch, "E958", {"center": v(121.14, 108.26) * mm, "radius": 0.76 * mm});
            skCircle(sketch, "E959", {"center": v(118.6, 105.72) * mm, "radius": 0.76 * mm});
            skCircle(sketch, "E960", {"center": v(121.14, 105.72) * mm, "radius": 0.76 * mm});
            skCircle(sketch, "E961", {"center": v(118.6, 103.18) * mm, "radius": 0.76 * mm});
            skCircle(sketch, "E962", {"center": v(121.14, 103.18) * mm, "radius": 0.76 * mm});
            skCircle(sketch, "E963", {"center": v(118.6, 100.64) * mm, "radius": 0.76 * mm});
            skCircle(sketch, "E964", {"center": v(121.14, 100.64) * mm, "radius": 0.76 * mm});
            skCircle(sketch, "E965", {"center": v(118.6, 98.1) * mm, "radius": 0.76 * mm});
            skCircle(sketch, "E966", {"center": v(121.14, 98.1) * mm, "radius": 0.76 * mm});
            skCircle(sketch, "E967", {"center": v(118.6, 95.56) * mm, "radius": 0.76 * mm});
            skCircle(sketch, "E968", {"center": v(121.14, 95.56) * mm, "radius": 0.76 * mm});
            skCircle(sketch, "E969", {"center": v(118.6, 93.02) * mm, "radius": 0.76 * mm});
            skCircle(sketch, "E970", {"center": v(121.14, 93.02) * mm, "radius": 0.76 * mm});
            skCircle(sketch, "E971", {"center": v(118.6, 90.48) * mm, "radius": 0.76 * mm});
            skCircle(sketch, "E972", {"center": v(121.14, 90.48) * mm, "radius": 0.76 * mm});
            skCircle(sketch, "E973", {"center": v(118.6, 87.94) * mm, "radius": 0.76 * mm});
            skCircle(sketch, "E974", {"center": v(121.14, 87.94) * mm, "radius": 0.76 * mm});
            skCircle(sketch, "E975", {"center": v(118.6, 85.4) * mm, "radius": 0.76 * mm});
            skCircle(sketch, "E976", {"center": v(121.14, 85.4) * mm, "radius": 0.76 * mm});
            skCircle(sketch, "E977", {"center": v(118.6, 82.86) * mm, "radius": 0.76 * mm});
            skCircle(sketch, "E978", {"center": v(121.14, 82.86) * mm, "radius": 0.76 * mm});
            skCircle(sketch, "E979", {"center": v(133.24, 131.12) * mm, "radius": 0.76 * mm});
            skCircle(sketch, "E980", {"center": v(130.7, 128.58) * mm, "radius": 0.76 * mm});
            skCircle(sketch, "E981", {"center": v(133.24, 128.58) * mm, "radius": 0.76 * mm});
            skCircle(sketch, "E982", {"center": v(130.7, 126.04) * mm, "radius": 0.76 * mm});
            skCircle(sketch, "E983", {"center": v(133.24, 126.04) * mm, "radius": 0.76 * mm});
            skCircle(sketch, "E984", {"center": v(130.7, 123.5) * mm, "radius": 0.76 * mm});
            skCircle(sketch, "E985", {"center": v(133.24, 123.5) * mm, "radius": 0.76 * mm});
            skCircle(sketch, "E986", {"center": v(130.7, 120.96) * mm, "radius": 0.76 * mm});
            skCircle(sketch, "E987", {"center": v(133.24, 120.96) * mm, "radius": 0.76 * mm});
            skCircle(sketch, "E988", {"center": v(130.7, 118.42) * mm, "radius": 0.76 * mm});
            skCircle(sketch, "E989", {"center": v(133.24, 118.42) * mm, "radius": 0.76 * mm});
            skCircle(sketch, "E990", {"center": v(130.7, 115.88) * mm, "radius": 0.76 * mm});
            skCircle(sketch, "E991", {"center": v(133.24, 115.88) * mm, "radius": 0.76 * mm});
            skCircle(sketch, "E992", {"center": v(130.7, 113.34) * mm, "radius": 0.76 * mm});
            skCircle(sketch, "E993", {"center": v(133.24, 113.34) * mm, "radius": 0.76 * mm});
            skCircle(sketch, "E994", {"center": v(130.7, 110.8) * mm, "radius": 0.76 * mm});
            skCircle(sketch, "E995", {"center": v(133.24, 110.8) * mm, "radius": 0.76 * mm});
            skCircle(sketch, "E996", {"center": v(130.7, 108.26) * mm, "radius": 0.76 * mm});
            skCircle(sketch, "E997", {"center": v(133.24, 108.26) * mm, "radius": 0.76 * mm});
            skCircle(sketch, "E998", {"center": v(130.7, 105.72) * mm, "radius": 0.76 * mm});
            skCircle(sketch, "E999", {"center": v(133.24, 105.72) * mm, "radius": 0.76 * mm});
            skCircle(sketch, "E1000", {"center": v(130.7, 103.18) * mm, "radius": 0.76 * mm});
            skCircle(sketch, "E1001", {"center": v(133.24, 103.18) * mm, "radius": 0.76 * mm});
            skCircle(sketch, "E1002", {"center": v(130.7, 100.64) * mm, "radius": 0.76 * mm});
            skCircle(sketch, "E1003", {"center": v(133.24, 100.64) * mm, "radius": 0.76 * mm});
            skCircle(sketch, "E1004", {"center": v(130.7, 98.1) * mm, "radius": 0.76 * mm});
            skCircle(sketch, "E1005", {"center": v(133.24, 98.1) * mm, "radius": 0.76 * mm});
            skCircle(sketch, "E1006", {"center": v(130.7, 95.56) * mm, "radius": 0.76 * mm});
            skCircle(sketch, "E1007", {"center": v(133.24, 95.56) * mm, "radius": 0.76 * mm});
            skCircle(sketch, "E1008", {"center": v(130.7, 93.02) * mm, "radius": 0.76 * mm});
            skCircle(sketch, "E1009", {"center": v(133.24, 93.02) * mm, "radius": 0.76 * mm});
            skCircle(sketch, "E1010", {"center": v(130.7, 90.48) * mm, "radius": 0.76 * mm});
            skCircle(sketch, "E1011", {"center": v(133.24, 90.48) * mm, "radius": 0.76 * mm});
            skCircle(sketch, "E1012", {"center": v(130.7, 87.94) * mm, "radius": 0.76 * mm});
            skCircle(sketch, "E1013", {"center": v(133.24, 87.94) * mm, "radius": 0.76 * mm});
            skCircle(sketch, "E1014", {"center": v(130.7, 85.4) * mm, "radius": 0.76 * mm});
            skCircle(sketch, "E1015", {"center": v(133.24, 85.4) * mm, "radius": 0.76 * mm});
            skCircle(sketch, "E1016", {"center": v(130.7, 82.86) * mm, "radius": 0.76 * mm});
            skCircle(sketch, "E1017", {"center": v(133.24, 82.86) * mm, "radius": 0.76 * mm});
            skCircle(sketch, "E1018", {"center": v(145.34, 131.12) * mm, "radius": 0.76 * mm});
            skCircle(sketch, "E1019", {"center": v(142.8, 128.58) * mm, "radius": 0.76 * mm});
            skCircle(sketch, "E1020", {"center": v(145.34, 128.58) * mm, "radius": 0.76 * mm});
            skCircle(sketch, "E1021", {"center": v(142.8, 126.04) * mm, "radius": 0.76 * mm});
            skCircle(sketch, "E1022", {"center": v(145.34, 126.04) * mm, "radius": 0.76 * mm});
            skCircle(sketch, "E1023", {"center": v(142.8, 123.5) * mm, "radius": 0.76 * mm});
            skCircle(sketch, "E1024", {"center": v(145.34, 123.5) * mm, "radius": 0.76 * mm});
            skCircle(sketch, "E1025", {"center": v(142.8, 120.96) * mm, "radius": 0.76 * mm});
            skCircle(sketch, "E1026", {"center": v(145.34, 120.96) * mm, "radius": 0.76 * mm});
            skCircle(sketch, "E1027", {"center": v(142.8, 118.42) * mm, "radius": 0.76 * mm});
            skCircle(sketch, "E1028", {"center": v(145.34, 118.42) * mm, "radius": 0.76 * mm});
            skCircle(sketch, "E1029", {"center": v(142.8, 115.88) * mm, "radius": 0.76 * mm});
            skCircle(sketch, "E1030", {"center": v(145.34, 115.88) * mm, "radius": 0.76 * mm});
            skCircle(sketch, "E1031", {"center": v(142.8, 113.34) * mm, "radius": 0.76 * mm});
            skCircle(sketch, "E1032", {"center": v(145.34, 113.34) * mm, "radius": 0.76 * mm});
            skCircle(sketch, "E1033", {"center": v(142.8, 110.8) * mm, "radius": 0.76 * mm});
            skCircle(sketch, "E1034", {"center": v(145.34, 110.8) * mm, "radius": 0.76 * mm});
            skCircle(sketch, "E1035", {"center": v(142.8, 108.26) * mm, "radius": 0.76 * mm});
            skCircle(sketch, "E1036", {"center": v(145.34, 108.26) * mm, "radius": 0.76 * mm});
            skCircle(sketch, "E1037", {"center": v(142.8, 105.72) * mm, "radius": 0.76 * mm});
            skCircle(sketch, "E1038", {"center": v(145.34, 105.72) * mm, "radius": 0.76 * mm});
            skCircle(sketch, "E1039", {"center": v(142.8, 103.18) * mm, "radius": 0.76 * mm});
            skCircle(sketch, "E1040", {"center": v(145.34, 103.18) * mm, "radius": 0.76 * mm});
            skCircle(sketch, "E1041", {"center": v(142.8, 100.64) * mm, "radius": 0.76 * mm});
            skCircle(sketch, "E1042", {"center": v(145.34, 100.64) * mm, "radius": 0.76 * mm});
            skCircle(sketch, "E1043", {"center": v(142.8, 98.1) * mm, "radius": 0.76 * mm});
            skCircle(sketch, "E1044", {"center": v(145.34, 98.1) * mm, "radius": 0.76 * mm});
            skCircle(sketch, "E1045", {"center": v(142.8, 95.56) * mm, "radius": 0.76 * mm});
            skCircle(sketch, "E1046", {"center": v(145.34, 95.56) * mm, "radius": 0.76 * mm});
            skCircle(sketch, "E1047", {"center": v(142.8, 93.02) * mm, "radius": 0.76 * mm});
            skCircle(sketch, "E1048", {"center": v(145.34, 93.02) * mm, "radius": 0.76 * mm});
            skCircle(sketch, "E1049", {"center": v(142.8, 90.48) * mm, "radius": 0.76 * mm});
            skCircle(sketch, "E1050", {"center": v(145.34, 90.48) * mm, "radius": 0.76 * mm});
            skCircle(sketch, "E1051", {"center": v(142.8, 87.94) * mm, "radius": 0.76 * mm});
            skCircle(sketch, "E1052", {"center": v(145.34, 87.94) * mm, "radius": 0.76 * mm});
            skCircle(sketch, "E1053", {"center": v(142.8, 85.4) * mm, "radius": 0.76 * mm});
            skCircle(sketch, "E1054", {"center": v(145.34, 85.4) * mm, "radius": 0.76 * mm});
            skCircle(sketch, "E1055", {"center": v(142.8, 82.86) * mm, "radius": 0.76 * mm});
            skCircle(sketch, "E1056", {"center": v(145.34, 82.86) * mm, "radius": 0.76 * mm});
            skCircle(sketch, "E1057", {"center": v(-84.56, 131.12) * mm, "radius": 0.76 * mm});
            skCircle(sketch, "E1058", {"center": v(-87.1, 128.58) * mm, "radius": 0.76 * mm});
            skCircle(sketch, "E1059", {"center": v(-84.56, 128.58) * mm, "radius": 0.76 * mm});
            skCircle(sketch, "E1060", {"center": v(-87.1, 126.04) * mm, "radius": 0.76 * mm});
            skCircle(sketch, "E1061", {"center": v(-84.56, 126.04) * mm, "radius": 0.76 * mm});
            skCircle(sketch, "E1062", {"center": v(-87.1, 123.5) * mm, "radius": 0.76 * mm});
            skCircle(sketch, "E1063", {"center": v(-84.56, 123.5) * mm, "radius": 0.76 * mm});
            skCircle(sketch, "E1064", {"center": v(-87.1, 120.96) * mm, "radius": 0.76 * mm});
            skCircle(sketch, "E1065", {"center": v(-84.56, 120.96) * mm, "radius": 0.76 * mm});
            skCircle(sketch, "E1066", {"center": v(-87.1, 118.42) * mm, "radius": 0.76 * mm});
            skCircle(sketch, "E1067", {"center": v(-84.56, 118.42) * mm, "radius": 0.76 * mm});
            skCircle(sketch, "E1068", {"center": v(-87.1, 115.88) * mm, "radius": 0.76 * mm});
            skCircle(sketch, "E1069", {"center": v(-84.56, 115.88) * mm, "radius": 0.76 * mm});
            skCircle(sketch, "E1070", {"center": v(-87.1, 113.34) * mm, "radius": 0.76 * mm});
            skCircle(sketch, "E1071", {"center": v(-84.56, 113.34) * mm, "radius": 0.76 * mm});
            skCircle(sketch, "E1072", {"center": v(-87.1, 110.8) * mm, "radius": 0.76 * mm});
            skCircle(sketch, "E1073", {"center": v(-84.56, 110.8) * mm, "radius": 0.76 * mm});
            skCircle(sketch, "E1074", {"center": v(-87.1, 108.26) * mm, "radius": 0.76 * mm});
            skCircle(sketch, "E1075", {"center": v(-84.56, 108.26) * mm, "radius": 0.76 * mm});
            skCircle(sketch, "E1076", {"center": v(-87.1, 105.72) * mm, "radius": 0.76 * mm});
            skCircle(sketch, "E1077", {"center": v(-84.56, 105.72) * mm, "radius": 0.76 * mm});
            skCircle(sketch, "E1078", {"center": v(-87.1, 103.18) * mm, "radius": 0.76 * mm});
            skCircle(sketch, "E1079", {"center": v(-84.56, 103.18) * mm, "radius": 0.76 * mm});
            skCircle(sketch, "E1080", {"center": v(-87.1, 100.64) * mm, "radius": 0.76 * mm});
            skCircle(sketch, "E1081", {"center": v(-84.56, 100.64) * mm, "radius": 0.76 * mm});
            skCircle(sketch, "E1082", {"center": v(-87.1, 98.1) * mm, "radius": 0.76 * mm});
            skCircle(sketch, "E1083", {"center": v(-84.56, 98.1) * mm, "radius": 0.76 * mm});
            skCircle(sketch, "E1084", {"center": v(-87.1, 95.56) * mm, "radius": 0.76 * mm});
            skCircle(sketch, "E1085", {"center": v(-84.56, 95.56) * mm, "radius": 0.76 * mm});
            skCircle(sketch, "E1086", {"center": v(-87.1, 93.02) * mm, "radius": 0.76 * mm});
            skCircle(sketch, "E1087", {"center": v(-84.56, 93.02) * mm, "radius": 0.76 * mm});
            skCircle(sketch, "E1088", {"center": v(-87.1, 90.48) * mm, "radius": 0.76 * mm});
            skCircle(sketch, "E1089", {"center": v(-84.56, 90.48) * mm, "radius": 0.76 * mm});
            skCircle(sketch, "E1090", {"center": v(-87.1, 87.94) * mm, "radius": 0.76 * mm});
            skCircle(sketch, "E1091", {"center": v(-84.56, 87.94) * mm, "radius": 0.76 * mm});
            skCircle(sketch, "E1092", {"center": v(-87.1, 85.4) * mm, "radius": 0.76 * mm});
            skCircle(sketch, "E1093", {"center": v(-84.56, 85.4) * mm, "radius": 0.76 * mm});
            skCircle(sketch, "E1094", {"center": v(-87.1, 82.86) * mm, "radius": 0.76 * mm});
            skCircle(sketch, "E1095", {"center": v(-84.56, 82.86) * mm, "radius": 0.76 * mm});
            skCircle(sketch, "E1096", {"center": v(-108.76, 131.12) * mm, "radius": 0.76 * mm});
            skCircle(sketch, "E1097", {"center": v(-111.3, 128.58) * mm, "radius": 0.76 * mm});
            skCircle(sketch, "E1098", {"center": v(-108.76, 128.58) * mm, "radius": 0.76 * mm});
            skCircle(sketch, "E1099", {"center": v(-111.3, 126.04) * mm, "radius": 0.76 * mm});
            skCircle(sketch, "E1100", {"center": v(-108.76, 126.04) * mm, "radius": 0.76 * mm});
            skCircle(sketch, "E1101", {"center": v(-111.3, 123.5) * mm, "radius": 0.76 * mm});
            skCircle(sketch, "E1102", {"center": v(-108.76, 123.5) * mm, "radius": 0.76 * mm});
            skCircle(sketch, "E1103", {"center": v(-111.3, 120.96) * mm, "radius": 0.76 * mm});
            skCircle(sketch, "E1104", {"center": v(-108.76, 120.96) * mm, "radius": 0.76 * mm});
            skCircle(sketch, "E1105", {"center": v(-111.3, 118.42) * mm, "radius": 0.76 * mm});
            skCircle(sketch, "E1106", {"center": v(-108.76, 118.42) * mm, "radius": 0.76 * mm});
            skCircle(sketch, "E1107", {"center": v(-111.3, 115.88) * mm, "radius": 0.76 * mm});
            skCircle(sketch, "E1108", {"center": v(-108.76, 115.88) * mm, "radius": 0.76 * mm});
            skCircle(sketch, "E1109", {"center": v(-111.3, 113.34) * mm, "radius": 0.76 * mm});
            skCircle(sketch, "E1110", {"center": v(-108.76, 113.34) * mm, "radius": 0.76 * mm});
            skCircle(sketch, "E1111", {"center": v(-111.3, 110.8) * mm, "radius": 0.76 * mm});
            skCircle(sketch, "E1112", {"center": v(-108.76, 110.8) * mm, "radius": 0.76 * mm});
            skCircle(sketch, "E1113", {"center": v(-111.3, 108.26) * mm, "radius": 0.76 * mm});
            skCircle(sketch, "E1114", {"center": v(-108.76, 108.26) * mm, "radius": 0.76 * mm});
            skCircle(sketch, "E1115", {"center": v(-111.3, 105.72) * mm, "radius": 0.76 * mm});
            skCircle(sketch, "E1116", {"center": v(-108.76, 105.72) * mm, "radius": 0.76 * mm});
            skCircle(sketch, "E1117", {"center": v(-111.3, 103.18) * mm, "radius": 0.76 * mm});
            skCircle(sketch, "E1118", {"center": v(-108.76, 103.18) * mm, "radius": 0.76 * mm});
            skCircle(sketch, "E1119", {"center": v(-111.3, 100.64) * mm, "radius": 0.76 * mm});
            skCircle(sketch, "E1120", {"center": v(-108.76, 100.64) * mm, "radius": 0.76 * mm});
            skCircle(sketch, "E1121", {"center": v(-111.3, 98.1) * mm, "radius": 0.76 * mm});
            skCircle(sketch, "E1122", {"center": v(-108.76, 98.1) * mm, "radius": 0.76 * mm});
            skCircle(sketch, "E1123", {"center": v(-111.3, 95.56) * mm, "radius": 0.76 * mm});
            skCircle(sketch, "E1124", {"center": v(-108.76, 95.56) * mm, "radius": 0.76 * mm});
            skCircle(sketch, "E1125", {"center": v(-111.3, 93.02) * mm, "radius": 0.76 * mm});
            skCircle(sketch, "E1126", {"center": v(-108.76, 93.02) * mm, "radius": 0.76 * mm});
            skCircle(sketch, "E1127", {"center": v(-111.3, 90.48) * mm, "radius": 0.76 * mm});
            skCircle(sketch, "E1128", {"center": v(-108.76, 90.48) * mm, "radius": 0.76 * mm});
            skCircle(sketch, "E1129", {"center": v(-111.3, 87.94) * mm, "radius": 0.76 * mm});
            skCircle(sketch, "E1130", {"center": v(-108.76, 87.94) * mm, "radius": 0.76 * mm});
            skCircle(sketch, "E1131", {"center": v(-111.3, 85.4) * mm, "radius": 0.76 * mm});
            skCircle(sketch, "E1132", {"center": v(-108.76, 85.4) * mm, "radius": 0.76 * mm});
            skCircle(sketch, "E1133", {"center": v(-111.3, 82.86) * mm, "radius": 0.76 * mm});
            skCircle(sketch, "E1134", {"center": v(-108.76, 82.86) * mm, "radius": 0.76 * mm});
            skCircle(sketch, "E1135", {"center": v(-72.46, 131.12) * mm, "radius": 0.76 * mm});
            skCircle(sketch, "E1136", {"center": v(-75, 128.58) * mm, "radius": 0.76 * mm});
            skCircle(sketch, "E1137", {"center": v(-72.46, 128.58) * mm, "radius": 0.76 * mm});
            skCircle(sketch, "E1138", {"center": v(-75, 126.04) * mm, "radius": 0.76 * mm});
            skCircle(sketch, "E1139", {"center": v(-72.46, 126.04) * mm, "radius": 0.76 * mm});
            skCircle(sketch, "E1140", {"center": v(-75, 123.5) * mm, "radius": 0.76 * mm});
            skCircle(sketch, "E1141", {"center": v(-72.46, 123.5) * mm, "radius": 0.76 * mm});
            skCircle(sketch, "E1142", {"center": v(-75, 120.96) * mm, "radius": 0.76 * mm});
            skCircle(sketch, "E1143", {"center": v(-72.46, 120.96) * mm, "radius": 0.76 * mm});
            skCircle(sketch, "E1144", {"center": v(-75, 118.42) * mm, "radius": 0.76 * mm});
            skCircle(sketch, "E1145", {"center": v(-72.46, 118.42) * mm, "radius": 0.76 * mm});
            skCircle(sketch, "E1146", {"center": v(-75, 115.88) * mm, "radius": 0.76 * mm});
            skCircle(sketch, "E1147", {"center": v(-72.46, 115.88) * mm, "radius": 0.76 * mm});
            skCircle(sketch, "E1148", {"center": v(-75, 113.34) * mm, "radius": 0.76 * mm});
            skCircle(sketch, "E1149", {"center": v(-72.46, 113.34) * mm, "radius": 0.76 * mm});
            skCircle(sketch, "E1150", {"center": v(-75, 110.8) * mm, "radius": 0.76 * mm});
            skCircle(sketch, "E1151", {"center": v(-72.46, 110.8) * mm, "radius": 0.76 * mm});
            skCircle(sketch, "E1152", {"center": v(-75, 108.26) * mm, "radius": 0.76 * mm});
            skCircle(sketch, "E1153", {"center": v(-72.46, 108.26) * mm, "radius": 0.76 * mm});
            skCircle(sketch, "E1154", {"center": v(-75, 105.72) * mm, "radius": 0.76 * mm});
            skCircle(sketch, "E1155", {"center": v(-72.46, 105.72) * mm, "radius": 0.76 * mm});
            skCircle(sketch, "E1156", {"center": v(-75, 103.18) * mm, "radius": 0.76 * mm});
            skCircle(sketch, "E1157", {"center": v(-72.46, 103.18) * mm, "radius": 0.76 * mm});
            skCircle(sketch, "E1158", {"center": v(-75, 100.64) * mm, "radius": 0.76 * mm});
            skCircle(sketch, "E1159", {"center": v(-72.46, 100.64) * mm, "radius": 0.76 * mm});
            skCircle(sketch, "E1160", {"center": v(-75, 98.1) * mm, "radius": 0.76 * mm});
            skCircle(sketch, "E1161", {"center": v(-72.46, 98.1) * mm, "radius": 0.76 * mm});
            skCircle(sketch, "E1162", {"center": v(-75, 95.56) * mm, "radius": 0.76 * mm});
            skCircle(sketch, "E1163", {"center": v(-72.46, 95.56) * mm, "radius": 0.76 * mm});
            skCircle(sketch, "E1164", {"center": v(-75, 93.02) * mm, "radius": 0.76 * mm});
            skCircle(sketch, "E1165", {"center": v(-72.46, 93.02) * mm, "radius": 0.76 * mm});
            skCircle(sketch, "E1166", {"center": v(-75, 90.48) * mm, "radius": 0.76 * mm});
            skCircle(sketch, "E1167", {"center": v(-72.46, 90.48) * mm, "radius": 0.76 * mm});
            skCircle(sketch, "E1168", {"center": v(-75, 87.94) * mm, "radius": 0.76 * mm});
            skCircle(sketch, "E1169", {"center": v(-72.46, 87.94) * mm, "radius": 0.76 * mm});
            skCircle(sketch, "E1170", {"center": v(-75, 85.4) * mm, "radius": 0.76 * mm});
            skCircle(sketch, "E1171", {"center": v(-72.46, 85.4) * mm, "radius": 0.76 * mm});
            skCircle(sketch, "E1172", {"center": v(-75, 82.86) * mm, "radius": 0.76 * mm});
            skCircle(sketch, "E1173", {"center": v(-72.46, 82.86) * mm, "radius": 0.76 * mm});
            skCircle(sketch, "E1174", {"center": v(-60.36, 131.12) * mm, "radius": 0.76 * mm});
            skCircle(sketch, "E1175", {"center": v(-62.9, 128.58) * mm, "radius": 0.76 * mm});
            skCircle(sketch, "E1176", {"center": v(-60.36, 128.58) * mm, "radius": 0.76 * mm});
            skCircle(sketch, "E1177", {"center": v(-62.9, 126.04) * mm, "radius": 0.76 * mm});
            skCircle(sketch, "E1178", {"center": v(-60.36, 126.04) * mm, "radius": 0.76 * mm});
            skCircle(sketch, "E1179", {"center": v(-62.9, 123.5) * mm, "radius": 0.76 * mm});
            skCircle(sketch, "E1180", {"center": v(-60.36, 123.5) * mm, "radius": 0.76 * mm});
            skCircle(sketch, "E1181", {"center": v(-62.9, 120.96) * mm, "radius": 0.76 * mm});
            skCircle(sketch, "E1182", {"center": v(-60.36, 120.96) * mm, "radius": 0.76 * mm});
            skCircle(sketch, "E1183", {"center": v(-62.9, 118.42) * mm, "radius": 0.76 * mm});
            skCircle(sketch, "E1184", {"center": v(-60.36, 118.42) * mm, "radius": 0.76 * mm});
            skCircle(sketch, "E1185", {"center": v(-62.9, 115.88) * mm, "radius": 0.76 * mm});
            skCircle(sketch, "E1186", {"center": v(-60.36, 115.88) * mm, "radius": 0.76 * mm});
            skCircle(sketch, "E1187", {"center": v(-62.9, 113.34) * mm, "radius": 0.76 * mm});
            skCircle(sketch, "E1188", {"center": v(-60.36, 113.34) * mm, "radius": 0.76 * mm});
            skCircle(sketch, "E1189", {"center": v(-62.9, 110.8) * mm, "radius": 0.76 * mm});
            skCircle(sketch, "E1190", {"center": v(-60.36, 110.8) * mm, "radius": 0.76 * mm});
            skCircle(sketch, "E1191", {"center": v(-62.9, 108.26) * mm, "radius": 0.76 * mm});
            skCircle(sketch, "E1192", {"center": v(-60.36, 108.26) * mm, "radius": 0.76 * mm});
            skCircle(sketch, "E1193", {"center": v(-62.9, 105.72) * mm, "radius": 0.76 * mm});
            skCircle(sketch, "E1194", {"center": v(-60.36, 105.72) * mm, "radius": 0.76 * mm});
            skCircle(sketch, "E1195", {"center": v(-62.9, 103.18) * mm, "radius": 0.76 * mm});
            skCircle(sketch, "E1196", {"center": v(-60.36, 103.18) * mm, "radius": 0.76 * mm});
            skCircle(sketch, "E1197", {"center": v(-62.9, 100.64) * mm, "radius": 0.76 * mm});
            skCircle(sketch, "E1198", {"center": v(-60.36, 100.64) * mm, "radius": 0.76 * mm});
            skCircle(sketch, "E1199", {"center": v(-62.9, 98.1) * mm, "radius": 0.76 * mm});
            skCircle(sketch, "E1200", {"center": v(-60.36, 98.1) * mm, "radius": 0.76 * mm});
            skCircle(sketch, "E1201", {"center": v(-62.9, 95.56) * mm, "radius": 0.76 * mm});
            skCircle(sketch, "E1202", {"center": v(-60.36, 95.56) * mm, "radius": 0.76 * mm});
            skCircle(sketch, "E1203", {"center": v(-62.9, 93.02) * mm, "radius": 0.76 * mm});
            skCircle(sketch, "E1204", {"center": v(-60.36, 93.02) * mm, "radius": 0.76 * mm});
            skCircle(sketch, "E1205", {"center": v(-62.9, 90.48) * mm, "radius": 0.76 * mm});
            skCircle(sketch, "E1206", {"center": v(-60.36, 90.48) * mm, "radius": 0.76 * mm});
            skCircle(sketch, "E1207", {"center": v(-62.9, 87.94) * mm, "radius": 0.76 * mm});
            skCircle(sketch, "E1208", {"center": v(-60.36, 87.94) * mm, "radius": 0.76 * mm});
            skCircle(sketch, "E1209", {"center": v(-62.9, 85.4) * mm, "radius": 0.76 * mm});
            skCircle(sketch, "E1210", {"center": v(-60.36, 85.4) * mm, "radius": 0.76 * mm});
            skCircle(sketch, "E1211", {"center": v(-62.9, 82.86) * mm, "radius": 0.76 * mm});
            skCircle(sketch, "E1212", {"center": v(-60.36, 82.86) * mm, "radius": 0.76 * mm});
            skCircle(sketch, "E1213", {"center": v(-48.26, 131.12) * mm, "radius": 0.76 * mm});
            skCircle(sketch, "E1214", {"center": v(-50.8, 128.58) * mm, "radius": 0.76 * mm});
            skCircle(sketch, "E1215", {"center": v(-48.26, 128.58) * mm, "radius": 0.76 * mm});
            skCircle(sketch, "E1216", {"center": v(-50.8, 126.04) * mm, "radius": 0.76 * mm});
            skCircle(sketch, "E1217", {"center": v(-48.26, 126.04) * mm, "radius": 0.76 * mm});
            skCircle(sketch, "E1218", {"center": v(-50.8, 123.5) * mm, "radius": 0.76 * mm});
            skCircle(sketch, "E1219", {"center": v(-48.26, 123.5) * mm, "radius": 0.76 * mm});
            skCircle(sketch, "E1220", {"center": v(-50.8, 120.96) * mm, "radius": 0.76 * mm});
            skCircle(sketch, "E1221", {"center": v(-48.26, 120.96) * mm, "radius": 0.76 * mm});
            skCircle(sketch, "E1222", {"center": v(-50.8, 118.42) * mm, "radius": 0.76 * mm});
            skCircle(sketch, "E1223", {"center": v(-48.26, 118.42) * mm, "radius": 0.76 * mm});
            skCircle(sketch, "E1224", {"center": v(-50.8, 115.88) * mm, "radius": 0.76 * mm});
            skCircle(sketch, "E1225", {"center": v(-48.26, 115.88) * mm, "radius": 0.76 * mm});
            skCircle(sketch, "E1226", {"center": v(-50.8, 113.34) * mm, "radius": 0.76 * mm});
            skCircle(sketch, "E1227", {"center": v(-48.26, 113.34) * mm, "radius": 0.76 * mm});
            skCircle(sketch, "E1228", {"center": v(-50.8, 110.8) * mm, "radius": 0.76 * mm});
            skCircle(sketch, "E1229", {"center": v(-48.26, 110.8) * mm, "radius": 0.76 * mm});
            skCircle(sketch, "E1230", {"center": v(-50.8, 108.26) * mm, "radius": 0.76 * mm});
            skCircle(sketch, "E1231", {"center": v(-48.26, 108.26) * mm, "radius": 0.76 * mm});
            skCircle(sketch, "E1232", {"center": v(-50.8, 105.72) * mm, "radius": 0.76 * mm});
            skCircle(sketch, "E1233", {"center": v(-48.26, 105.72) * mm, "radius": 0.76 * mm});
            skCircle(sketch, "E1234", {"center": v(-50.8, 103.18) * mm, "radius": 0.76 * mm});
            skCircle(sketch, "E1235", {"center": v(-48.26, 103.18) * mm, "radius": 0.76 * mm});
            skCircle(sketch, "E1236", {"center": v(-50.8, 100.64) * mm, "radius": 0.76 * mm});
            skCircle(sketch, "E1237", {"center": v(-48.26, 100.64) * mm, "radius": 0.76 * mm});
            skCircle(sketch, "E1238", {"center": v(-50.8, 98.1) * mm, "radius": 0.76 * mm});
            skCircle(sketch, "E1239", {"center": v(-48.26, 98.1) * mm, "radius": 0.76 * mm});
            skCircle(sketch, "E1240", {"center": v(-50.8, 95.56) * mm, "radius": 0.76 * mm});
            skCircle(sketch, "E1241", {"center": v(-48.26, 95.56) * mm, "radius": 0.76 * mm});
            skCircle(sketch, "E1242", {"center": v(-50.8, 93.02) * mm, "radius": 0.76 * mm});
            skCircle(sketch, "E1243", {"center": v(-48.26, 93.02) * mm, "radius": 0.76 * mm});
            skCircle(sketch, "E1244", {"center": v(-50.8, 90.48) * mm, "radius": 0.76 * mm});
            skCircle(sketch, "E1245", {"center": v(-48.26, 90.48) * mm, "radius": 0.76 * mm});
            skCircle(sketch, "E1246", {"center": v(-50.8, 87.94) * mm, "radius": 0.76 * mm});
            skCircle(sketch, "E1247", {"center": v(-48.26, 87.94) * mm, "radius": 0.76 * mm});
            skCircle(sketch, "E1248", {"center": v(-50.8, 85.4) * mm, "radius": 0.76 * mm});
            skCircle(sketch, "E1249", {"center": v(-48.26, 85.4) * mm, "radius": 0.76 * mm});
            skCircle(sketch, "E1250", {"center": v(-50.8, 82.86) * mm, "radius": 0.76 * mm});
            skCircle(sketch, "E1251", {"center": v(-48.26, 82.86) * mm, "radius": 0.76 * mm});
            skCircle(sketch, "E1252", {"center": v(-36.16, 131.12) * mm, "radius": 0.76 * mm});
            skCircle(sketch, "E1253", {"center": v(-38.7, 128.58) * mm, "radius": 0.76 * mm});
            skCircle(sketch, "E1254", {"center": v(-36.16, 128.58) * mm, "radius": 0.76 * mm});
            skCircle(sketch, "E1255", {"center": v(-38.7, 126.04) * mm, "radius": 0.76 * mm});
            skCircle(sketch, "E1256", {"center": v(-36.16, 126.04) * mm, "radius": 0.76 * mm});
            skCircle(sketch, "E1257", {"center": v(-38.7, 123.5) * mm, "radius": 0.76 * mm});
            skCircle(sketch, "E1258", {"center": v(-36.16, 123.5) * mm, "radius": 0.76 * mm});
            skCircle(sketch, "E1259", {"center": v(-38.7, 120.96) * mm, "radius": 0.76 * mm});
            skCircle(sketch, "E1260", {"center": v(-36.16, 120.96) * mm, "radius": 0.76 * mm});
            skCircle(sketch, "E1261", {"center": v(-38.7, 118.42) * mm, "radius": 0.76 * mm});
            skCircle(sketch, "E1262", {"center": v(-36.16, 118.42) * mm, "radius": 0.76 * mm});
            skCircle(sketch, "E1263", {"center": v(-38.7, 115.88) * mm, "radius": 0.76 * mm});
            skCircle(sketch, "E1264", {"center": v(-36.16, 115.88) * mm, "radius": 0.76 * mm});
            skCircle(sketch, "E1265", {"center": v(-38.7, 113.34) * mm, "radius": 0.76 * mm});
            skCircle(sketch, "E1266", {"center": v(-36.16, 113.34) * mm, "radius": 0.76 * mm});
            skCircle(sketch, "E1267", {"center": v(-38.7, 110.8) * mm, "radius": 0.76 * mm});
            skCircle(sketch, "E1268", {"center": v(-36.16, 110.8) * mm, "radius": 0.76 * mm});
            skCircle(sketch, "E1269", {"center": v(-38.7, 108.26) * mm, "radius": 0.76 * mm});
            skCircle(sketch, "E1270", {"center": v(-36.16, 108.26) * mm, "radius": 0.76 * mm});
            skCircle(sketch, "E1271", {"center": v(-38.7, 105.72) * mm, "radius": 0.76 * mm});
            skCircle(sketch, "E1272", {"center": v(-36.16, 105.72) * mm, "radius": 0.76 * mm});
            skCircle(sketch, "E1273", {"center": v(-38.7, 103.18) * mm, "radius": 0.76 * mm});
            skCircle(sketch, "E1274", {"center": v(-36.16, 103.18) * mm, "radius": 0.76 * mm});
            skCircle(sketch, "E1275", {"center": v(-38.7, 100.64) * mm, "radius": 0.76 * mm});
            skCircle(sketch, "E1276", {"center": v(-36.16, 100.64) * mm, "radius": 0.76 * mm});
            skCircle(sketch, "E1277", {"center": v(-38.7, 98.1) * mm, "radius": 0.76 * mm});
            skCircle(sketch, "E1278", {"center": v(-36.16, 98.1) * mm, "radius": 0.76 * mm});
            skCircle(sketch, "E1279", {"center": v(-38.7, 95.56) * mm, "radius": 0.76 * mm});
            skCircle(sketch, "E1280", {"center": v(-36.16, 95.56) * mm, "radius": 0.76 * mm});
            skCircle(sketch, "E1281", {"center": v(-38.7, 93.02) * mm, "radius": 0.76 * mm});
            skCircle(sketch, "E1282", {"center": v(-36.16, 93.02) * mm, "radius": 0.76 * mm});
            skCircle(sketch, "E1283", {"center": v(-38.7, 90.48) * mm, "radius": 0.76 * mm});
            skCircle(sketch, "E1284", {"center": v(-36.16, 90.48) * mm, "radius": 0.76 * mm});
            skCircle(sketch, "E1285", {"center": v(-38.7, 87.94) * mm, "radius": 0.76 * mm});
            skCircle(sketch, "E1286", {"center": v(-36.16, 87.94) * mm, "radius": 0.76 * mm});
            skCircle(sketch, "E1287", {"center": v(-38.7, 85.4) * mm, "radius": 0.76 * mm});
            skCircle(sketch, "E1288", {"center": v(-36.16, 85.4) * mm, "radius": 0.76 * mm});
            skCircle(sketch, "E1289", {"center": v(-38.7, 82.86) * mm, "radius": 0.76 * mm});
            skCircle(sketch, "E1290", {"center": v(-36.16, 82.86) * mm, "radius": 0.76 * mm});
            skCircle(sketch, "E1291", {"center": v(-24.06, 131.12) * mm, "radius": 0.76 * mm});
            skCircle(sketch, "E1292", {"center": v(-26.6, 128.58) * mm, "radius": 0.76 * mm});
            skCircle(sketch, "E1293", {"center": v(-24.06, 128.58) * mm, "radius": 0.76 * mm});
            skCircle(sketch, "E1294", {"center": v(-26.6, 126.04) * mm, "radius": 0.76 * mm});
            skCircle(sketch, "E1295", {"center": v(-24.06, 126.04) * mm, "radius": 0.76 * mm});
            skCircle(sketch, "E1296", {"center": v(-26.6, 123.5) * mm, "radius": 0.76 * mm});
            skCircle(sketch, "E1297", {"center": v(-24.06, 123.5) * mm, "radius": 0.76 * mm});
            skCircle(sketch, "E1298", {"center": v(-26.6, 120.96) * mm, "radius": 0.76 * mm});
            skCircle(sketch, "E1299", {"center": v(-24.06, 120.96) * mm, "radius": 0.76 * mm});
            skCircle(sketch, "E1300", {"center": v(-26.6, 118.42) * mm, "radius": 0.76 * mm});
            skCircle(sketch, "E1301", {"center": v(-24.06, 118.42) * mm, "radius": 0.76 * mm});
            skCircle(sketch, "E1302", {"center": v(-26.6, 115.88) * mm, "radius": 0.76 * mm});
            skCircle(sketch, "E1303", {"center": v(-24.06, 115.88) * mm, "radius": 0.76 * mm});
            skCircle(sketch, "E1304", {"center": v(-26.6, 113.34) * mm, "radius": 0.76 * mm});
            skCircle(sketch, "E1305", {"center": v(-24.06, 113.34) * mm, "radius": 0.76 * mm});
            skCircle(sketch, "E1306", {"center": v(-26.6, 110.8) * mm, "radius": 0.76 * mm});
            skCircle(sketch, "E1307", {"center": v(-24.06, 110.8) * mm, "radius": 0.76 * mm});
            skCircle(sketch, "E1308", {"center": v(-26.6, 108.26) * mm, "radius": 0.76 * mm});
            skCircle(sketch, "E1309", {"center": v(-24.06, 108.26) * mm, "radius": 0.76 * mm});
            skCircle(sketch, "E1310", {"center": v(-26.6, 105.72) * mm, "radius": 0.76 * mm});
            skCircle(sketch, "E1311", {"center": v(-24.06, 105.72) * mm, "radius": 0.76 * mm});
            skCircle(sketch, "E1312", {"center": v(-26.6, 103.18) * mm, "radius": 0.76 * mm});
            skCircle(sketch, "E1313", {"center": v(-24.06, 103.18) * mm, "radius": 0.76 * mm});
            skCircle(sketch, "E1314", {"center": v(-26.6, 100.64) * mm, "radius": 0.76 * mm});
            skCircle(sketch, "E1315", {"center": v(-24.06, 100.64) * mm, "radius": 0.76 * mm});
            skCircle(sketch, "E1316", {"center": v(-26.6, 98.1) * mm, "radius": 0.76 * mm});
            skCircle(sketch, "E1317", {"center": v(-24.06, 98.1) * mm, "radius": 0.76 * mm});
            skCircle(sketch, "E1318", {"center": v(-26.6, 95.56) * mm, "radius": 0.76 * mm});
            skCircle(sketch, "E1319", {"center": v(-24.06, 95.56) * mm, "radius": 0.76 * mm});
            skCircle(sketch, "E1320", {"center": v(-26.6, 93.02) * mm, "radius": 0.76 * mm});
            skCircle(sketch, "E1321", {"center": v(-24.06, 93.02) * mm, "radius": 0.76 * mm});
            skCircle(sketch, "E1322", {"center": v(-26.6, 90.48) * mm, "radius": 0.76 * mm});
            skCircle(sketch, "E1323", {"center": v(-24.06, 90.48) * mm, "radius": 0.76 * mm});
            skCircle(sketch, "E1324", {"center": v(-26.6, 87.94) * mm, "radius": 0.76 * mm});
            skCircle(sketch, "E1325", {"center": v(-24.06, 87.94) * mm, "radius": 0.76 * mm});
            skCircle(sketch, "E1326", {"center": v(-26.6, 85.4) * mm, "radius": 0.76 * mm});
            skCircle(sketch, "E1327", {"center": v(-24.06, 85.4) * mm, "radius": 0.76 * mm});
            skCircle(sketch, "E1328", {"center": v(-26.6, 82.86) * mm, "radius": 0.76 * mm});
            skCircle(sketch, "E1329", {"center": v(-24.06, 82.86) * mm, "radius": 0.76 * mm});
            skCircle(sketch, "E1330", {"center": v(-138, -4) * mm, "radius": 0.76 * mm});
            skCircle(sketch, "E1331", {"center": v(-138, -16.7) * mm, "radius": 0.76 * mm});
            skCircle(sketch, "E1332", {"center": v(-138, -82) * mm, "radius": 0.76 * mm});
            skCircle(sketch, "E1333", {"center": v(-138, -94.7) * mm, "radius": 0.76 * mm});
            skCircle(sketch, "E1334", {"center": v(-127, -128) * mm, "radius": 0.76 * mm});
            skCircle(sketch, "E1335", {"center": v(-127, -115.3) * mm, "radius": 0.76 * mm});
            skCircle(sketch, "E1336", {"center": v(-124, -128) * mm, "radius": 0.76 * mm});
            skCircle(sketch, "E1337", {"center": v(-124, -115.3) * mm, "radius": 0.76 * mm});
            skCircle(sketch, "E1338", {"center": v(-138, -36) * mm, "radius": 0.76 * mm});
            skCircle(sketch, "E1339", {"center": v(-138, -48.7) * mm, "radius": 0.76 * mm});
            skCircle(sketch, "E1340", {"center": v(-163, 16) * mm, "radius": 0.76 * mm});
            skCircle(sketch, "E1341", {"center": v(-163, 31.24) * mm, "radius": 0.76 * mm});
            skCircle(sketch, "E1342", {"center": v(-158, 16) * mm, "radius": 0.76 * mm});
            skCircle(sketch, "E1343", {"center": v(-158, 31.24) * mm, "radius": 0.76 * mm});
            skCircle(sketch, "E1344", {"center": v(-114, -131) * mm, "radius": 0.76 * mm});
            skCircle(sketch, "E1345", {"center": v(-114, -146.24) * mm, "radius": 0.76 * mm});
            skCircle(sketch, "E1346", {"center": v(-118, -131) * mm, "radius": 0.76 * mm});
            skCircle(sketch, "E1347", {"center": v(-118, -146.24) * mm, "radius": 0.76 * mm});
            skCircle(sketch, "E1348", {"center": v(-69.5, -15.8) * mm, "radius": 0.75 * mm});
            skCircle(sketch, "E1349", {"center": v(-51.5, -15.8) * mm, "radius": 0.75 * mm});
            skCircle(sketch, "E1350", {"center": v(-69.5, -39.8) * mm, "radius": 0.75 * mm});
            skCircle(sketch, "E1351", {"center": v(-80, -112.9) * mm, "radius": 0.75 * mm});
            skCircle(sketch, "E1352", {"center": v(3, -119.9) * mm, "radius": 0.75 * mm});
            skCircle(sketch, "E1353", {"center": v(21, -119.9) * mm, "radius": 0.75 * mm});
            skCircle(sketch, "E1354", {"center": v(39, -119.9) * mm, "radius": 0.75 * mm});
            skCircle(sketch, "E1355", {"center": v(61, -77.9) * mm, "radius": 0.75 * mm});
            skCircle(sketch, "E1356", {"center": v(82, -77.9) * mm, "radius": 0.75 * mm});
            skCircle(sketch, "E1357", {"center": v(61, -101.9) * mm, "radius": 0.75 * mm});
            skCircle(sketch, "E1358", {"center": v(82, -101.9) * mm, "radius": 0.75 * mm});
            skCircle(sketch, "E1359", {"center": v(61, -121.9) * mm, "radius": 0.75 * mm});
            skCircle(sketch, "E1360", {"center": v(82, -121.9) * mm, "radius": 0.75 * mm});
            skCircle(sketch, "E1361", {"center": v(46.5, -35) * mm, "radius": 0.75 * mm});
            skCircle(sketch, "E1362", {"center": v(-50, -131.9) * mm, "radius": 0.75 * mm});
            skCircle(sketch, "E1363", {"center": v(-14, -131.9) * mm, "radius": 0.75 * mm});
            skCircle(sketch, "E1364", {"center": v(-32, -131.9) * mm, "radius": 0.75 * mm});
            skCircle(sketch, "E1365", {"center": v(113, -105.9) * mm, "radius": 0.75 * mm});
            skCircle(sketch, "E1366", {"center": v(108, -105.9) * mm, "radius": 0.75 * mm});
            skCircle(sketch, "E1367", {"center": v(131, -105.9) * mm, "radius": 0.75 * mm});
            skCircle(sketch, "E1368", {"center": v(126, -105.9) * mm, "radius": 0.75 * mm});
            skCircle(sketch, "E1369", {"center": v(-123.43, 136) * mm, "radius": 2.55 * mm});
            skCircle(sketch, "E1370", {"center": v(-123.43, 77.99) * mm, "radius": 2.55 * mm});
            skCircle(sketch, "E1371", {"center": v(-14.53, 136) * mm, "radius": 2.55 * mm});
            skCircle(sketch, "E1372", {"center": v(-14.53, 77.99) * mm, "radius": 2.55 * mm});
            skCircle(sketch, "E1373", {"center": v(9.67, 136) * mm, "radius": 2.55 * mm});
            skCircle(sketch, "E1374", {"center": v(9.67, 77.99) * mm, "radius": 2.55 * mm});
            skCircle(sketch, "E1375", {"center": v(21.77, 136) * mm, "radius": 2.55 * mm});
            skCircle(sketch, "E1376", {"center": v(21.77, 77.99) * mm, "radius": 2.55 * mm});
            skCircle(sketch, "E1377", {"center": v(33.87, 136) * mm, "radius": 2.55 * mm});
            skCircle(sketch, "E1378", {"center": v(33.87, 77.99) * mm, "radius": 2.55 * mm});
            skCircle(sketch, "E1379", {"center": v(45.97, 136) * mm, "radius": 2.55 * mm});
            skCircle(sketch, "E1380", {"center": v(45.97, 77.99) * mm, "radius": 2.55 * mm});
            skCircle(sketch, "E1381", {"center": v(58.07, 136) * mm, "radius": 2.55 * mm});
            skCircle(sketch, "E1382", {"center": v(58.07, 77.99) * mm, "radius": 2.55 * mm});
            skCircle(sketch, "E1383", {"center": v(70.17, 136) * mm, "radius": 2.55 * mm});
            skCircle(sketch, "E1384", {"center": v(70.17, 77.99) * mm, "radius": 2.55 * mm});
            skCircle(sketch, "E1385", {"center": v(-2.43, 136) * mm, "radius": 2.55 * mm});
            skCircle(sketch, "E1386", {"center": v(-2.43, 77.99) * mm, "radius": 2.55 * mm});
            skCircle(sketch, "E1387", {"center": v(82.27, 136) * mm, "radius": 2.55 * mm});
            skCircle(sketch, "E1388", {"center": v(82.27, 77.99) * mm, "radius": 2.55 * mm});
            skCircle(sketch, "E1389", {"center": v(94.37, 136) * mm, "radius": 2.55 * mm});
            skCircle(sketch, "E1390", {"center": v(94.37, 77.99) * mm, "radius": 2.55 * mm});
            skCircle(sketch, "E1391", {"center": v(-99.23, 136) * mm, "radius": 2.55 * mm});
            skCircle(sketch, "E1392", {"center": v(-99.23, 77.99) * mm, "radius": 2.55 * mm});
            skCircle(sketch, "E1393", {"center": v(130.67, 136) * mm, "radius": 2.55 * mm});
            skCircle(sketch, "E1394", {"center": v(130.67, 77.99) * mm, "radius": 2.55 * mm});
            skCircle(sketch, "E1395", {"center": v(142.77, 136) * mm, "radius": 2.55 * mm});
            skCircle(sketch, "E1396", {"center": v(142.77, 77.99) * mm, "radius": 2.55 * mm});
            skCircle(sketch, "E1397", {"center": v(-87.13, 136) * mm, "radius": 2.55 * mm});
            skCircle(sketch, "E1398", {"center": v(-87.13, 77.99) * mm, "radius": 2.55 * mm});
            skCircle(sketch, "E1399", {"center": v(-75.03, 136) * mm, "radius": 2.55 * mm});
            skCircle(sketch, "E1400", {"center": v(-75.03, 77.99) * mm, "radius": 2.55 * mm});
            skCircle(sketch, "E1401", {"center": v(-62.93, 136) * mm, "radius": 2.55 * mm});
            skCircle(sketch, "E1402", {"center": v(-62.93, 77.99) * mm, "radius": 2.55 * mm});
            skCircle(sketch, "E1403", {"center": v(-50.83, 136) * mm, "radius": 2.55 * mm});
            skCircle(sketch, "E1404", {"center": v(-50.83, 77.99) * mm, "radius": 2.55 * mm});
            skCircle(sketch, "E1405", {"center": v(-38.73, 136) * mm, "radius": 2.55 * mm});
            skCircle(sketch, "E1406", {"center": v(-38.73, 77.99) * mm, "radius": 2.55 * mm});
            skCircle(sketch, "E1407", {"center": v(-26.63, 136) * mm, "radius": 2.55 * mm});
            skCircle(sketch, "E1408", {"center": v(-26.63, 77.99) * mm, "radius": 2.55 * mm});
            skCircle(sketch, "E1409", {"center": v(106.47, 136) * mm, "radius": 2.51 * mm});
            skCircle(sketch, "E1410", {"center": v(106.47, 77.99) * mm, "radius": 2.51 * mm});
            skCircle(sketch, "E1411", {"center": v(118.57, 136) * mm, "radius": 2.51 * mm});
            skCircle(sketch, "E1412", {"center": v(118.57, 77.99) * mm, "radius": 2.51 * mm});
            skCircle(sketch, "E1413", {"center": v(102.57, 116.79) * mm, "radius": 1.11 * mm});
            skCircle(sketch, "E1414", {"center": v(102.57, 105.6) * mm, "radius": 1.11 * mm});
            skCircle(sketch, "E1415", {"center": v(114.67, 116.79) * mm, "radius": 1.11 * mm});
            skCircle(sketch, "E1416", {"center": v(114.67, 105.6) * mm, "radius": 1.11 * mm});
            skCircle(sketch, "E1417", {"center": v(0, -145) * mm, "radius": 2.75 * mm});
            skCircle(sketch, "E1418", {"center": v(-84, -145) * mm, "radius": 2.75 * mm});
            skCircle(sketch, "E1419", {"center": v(-163, 5) * mm, "radius": 2.75 * mm});
            skCircle(sketch, "E1420", {"center": v(-84, 145) * mm, "radius": 2.75 * mm});
            skCircle(sketch, "E1421", {"center": v(84, -145) * mm, "radius": 2.75 * mm});
            skCircle(sketch, "E1422", {"center": v(163, 80) * mm, "radius": 2.75 * mm});
            skCircle(sketch, "E1423", {"center": v(163, 5) * mm, "radius": 2.75 * mm});
            skCircle(sketch, "E1424", {"center": v(163, -145) * mm, "radius": 2.75 * mm});
            skCircle(sketch, "E1425", {"center": v(163, -70) * mm, "radius": 2.75 * mm});
            skCircle(sketch, "E1426", {"center": v(163, 145) * mm, "radius": 2.75 * mm});
            skCircle(sketch, "E1427", {"center": v(-163, 80) * mm, "radius": 2.75 * mm});
            skCircle(sketch, "E1428", {"center": v(-163, 145) * mm, "radius": 2.75 * mm});
            skCircle(sketch, "E1429", {"center": v(-163, -70) * mm, "radius": 2.75 * mm});
            skCircle(sketch, "E1430", {"center": v(-163, -145) * mm, "radius": 2.75 * mm});
            skCircle(sketch, "E1431", {"center": v(0, 145) * mm, "radius": 2.75 * mm});
            skCircle(sketch, "E1432", {"center": v(84, 145) * mm, "radius": 2.75 * mm});
            skCircle(sketch, "E1433", {"center": v(-132.5, 26.6) * mm, "radius": 2.75 * mm});
            skCircle(sketch, "E1434", {"center": v(-92.5, 26.6) * mm, "radius": 2.75 * mm});
            skCircle(sketch, "E1435", {"center": v(-57.5, 26.6) * mm, "radius": 2.75 * mm});
            skCircle(sketch, "E1436", {"center": v(-17.5, 26.6) * mm, "radius": 2.75 * mm});
            skCircle(sketch, "E1437", {"center": v(17.5, 26.6) * mm, "radius": 2.75 * mm});
            skCircle(sketch, "E1438", {"center": v(57.5, 26.6) * mm, "radius": 2.75 * mm});
            skCircle(sketch, "E1439", {"center": v(92.5, 26.6) * mm, "radius": 2.75 * mm});
            skCircle(sketch, "E1440", {"center": v(132.5, 26.6) * mm, "radius": 2.75 * mm});
            skCircle(sketch, "E1441", {"center": v(0, 5) * mm, "radius": 2.75 * mm});
            skCircle(sketch, "E1442", {"center": v(-84, 5) * mm, "radius": 2.75 * mm});
            skCircle(sketch, "E1443", {"center": v(84, 5) * mm, "radius": 2.75 * mm});
            skLineSegment(sketch, "E1444", {"start": v(-168, -150) * mm, "end": v(168, -150) * mm});
            skLineSegment(sketch, "E1445", {"start": v(168, -150) * mm, "end": v(168, 150) * mm});
            skLineSegment(sketch, "E1446", {"start": v(168, 150) * mm, "end": v(-168, 150) * mm});
            skLineSegment(sketch, "E1447", {"start": v(-168, 150) * mm, "end": v(-168, -150) * mm});
            skSolve(sketch);
        }
        {
            var Q0;
            Q0 = qSketchRegion(id + "F0", true);
            extrude(context, id + "F1", {"entities" : qUnion([Q0]), "depth" : 1.6 * mm, "offsetDistance" : 25 * mm});
        }
    });
